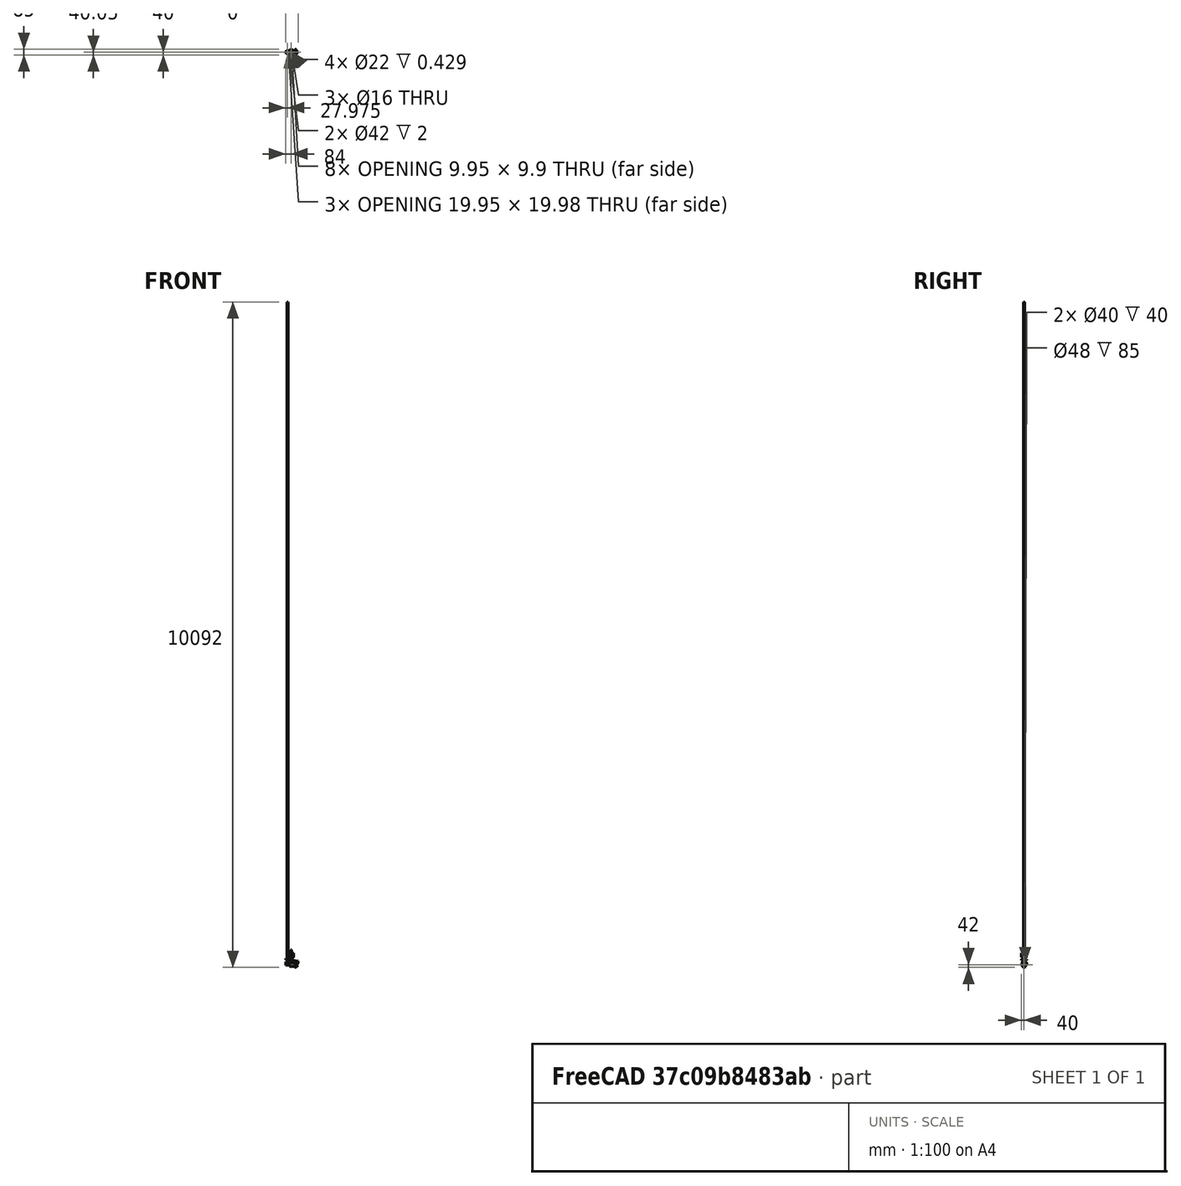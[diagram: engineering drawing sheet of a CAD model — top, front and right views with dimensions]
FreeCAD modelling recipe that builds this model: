
FCSTD DOCUMENT  (FreeCAD 0.16R6707 (Git))
Label: Mechanism-final
License: All rights reserved
LicenseURL: http://en.wikipedia.org/wiki/All_rights_reserved
objects: Sketcher::SketchObject×37, Part::Feature×23, PartDesign::Pad×16, App::DocumentObjectGroup×16, PartDesign::Revolution×13, Part::Sphere×10, Part::MultiFuse×9, Part::Cut×6, Part::Cylinder×4, Part::Part2DObjectPython×3, PartDesign::Pocket×1, Part::Sweep×1
note: 153 computed .brp shape members not serialized (recipe doc carries the construction recipe); baked Part::Feature solids carry a one-line shape summary decoded from their .brp

FEATURE [Part::Part2DObjectPython] InvoluteGear  # Draft 2D object (typed FeaturePython)
  ExternalGear = true
  HighPrecision = true
  Modules = 2.5
  NumberOfTeeth = 15
  Placement = pos=(0,0,20) rot=(0,0,1;0rad)
  PressureAngle = 20
FEATURE [PartDesign::Pad] Pad004  label="15-Teeth-Gear"
  Length = 10
  Length2 = 100
  Placement = pos=(0,0,20) rot=(0,0,1;0rad)
  Sketch = -> InvoluteGear
  Type = 0
FEATURE [Sketcher::SketchObject] Sketch004  label="15-Teeth-Gear-Hole-Sketch"
  Placement = pos=(0,0,20) rot=(1,0,0;3.14159rad)
  Support = -> Pad004 [Face151]
  sketch-geometry (4):
    g0: ArcOfCircle CenterX=0 CenterY=0 CenterZ=0 NormalX=0 NormalY=0 NormalZ=1 Radius=10 StartAngle=0.100167 EndAngle=6.18302
    g1: LineSegment StartX=9.94987 StartY=1 StartZ=0 EndX=8.94987 EndY=1 EndZ=0
    g2: LineSegment StartX=8.94987 StartY=1 StartZ=0 EndX=8.94987 EndY=-1 EndZ=0
    g3: LineSegment StartX=8.94987 StartY=-1 StartZ=0 EndX=9.94987 EndY=-1 EndZ=0
  constraints (12):
    c: Coincident(g0,g-1)
    c: Radius(g0) = 10
    c: Horizontal(g1)
    c: Coincident(g1,g2)
    c: Vertical(g2)
    c: Coincident(g2,g3)
    c: Symmetric(g1,g2,g-1)
    c: Horizontal(g3)
    c: Distance(g2) = 2
    c: Coincident(g0,g1)
    c: Coincident(g0,g3)
    c: Distance(g1) = 1
FEATURE [Sketcher::SketchObject] Sketch006  label="Main_Shaft_Sketch"
  Placement = pos=(0,0,0.5) rot=(0,0,1;0rad)
  sketch-geometry (4):
    g0: ArcOfCircle CenterX=0 CenterY=0 CenterZ=0 NormalX=0 NormalY=0 NormalZ=1 Radius=10 StartAngle=0.100167 EndAngle=6.18302
    g1: LineSegment StartX=9.94987 StartY=1 StartZ=0 EndX=8.94987 EndY=1 EndZ=0
    g2: LineSegment StartX=8.94987 StartY=1 StartZ=0 EndX=8.94987 EndY=-1 EndZ=0
    g3: LineSegment StartX=8.94987 StartY=-1 StartZ=0 EndX=9.94987 EndY=-1 EndZ=0
  constraints (12):
    c: Coincident(g0,g-1)
    c: Horizontal(g1)
    c: Coincident(g1,g2)
    c: Vertical(g2)
    c: Coincident(g2,g3)
    c: Horizontal(g3)
    c: Symmetric(g1,g2,g-1)
    c: Coincident(g0,g1)
    c: Coincident(g0,g3)
    c: Radius(g0) = 10
    c: DistanceX(g1,g1) = 1
    c: DistanceY(g2,g2) = 2
FEATURE [PartDesign::Pad] Pad005  label="Main_Shaft"
  Length = 90
  Length2 = 100
  Midplane = true
  Placement = pos=(0,0,0.5) rot=(0,0,1;0rad)
  Sketch = -> Sketch006
  Type = 0
FEATURE [Sketcher::SketchObject] Sketch007  label="Crank-Sketch"
  Placement = pos=(0,0,-35) rot=(0,0,1;0rad)
  sketch-geometry (10):
    g0: ArcOfCircle CenterX=0 CenterY=0 CenterZ=0 NormalX=0 NormalY=0 NormalZ=1 Radius=10 StartAngle=0.100167 EndAngle=6.18302
    g1: LineSegment StartX=9.94987 StartY=1 StartZ=0 EndX=8.94987 EndY=1 EndZ=0
    g2: LineSegment StartX=8.94987 StartY=1 StartZ=0 EndX=8.94987 EndY=-1 EndZ=0
    g3: LineSegment StartX=8.94987 StartY=-1 StartZ=0 EndX=9.94987 EndY=-1 EndZ=0
    g4: Circle CenterX=-20 CenterY=0 CenterZ=0 NormalX=0 NormalY=0 NormalZ=1 Radius=5
    g5: LineSegment [constr] StartX=-20 StartY=8 StartZ=0 EndX=-20 EndY=-8 EndZ=0
    g6: ArcOfCircle CenterX=-20 CenterY=0 CenterZ=0 NormalX=0 NormalY=0 NormalZ=1 Radius=8 StartAngle=1.5708 EndAngle=4.71239
    g7: ArcOfCircle CenterX=0 CenterY=0 CenterZ=0 NormalX=0 NormalY=0 NormalZ=1 Radius=20 StartAngle=4.71239 EndAngle=7.85398
    g8: ArcOfCircle CenterX=-24.2209 CenterY=37.7016 CenterZ=0 NormalX=0 NormalY=0 NormalZ=1 Radius=30 StartAngle=4.85356 EndAngle=5.65206
    g9: ArcOfCircle CenterX=-24.2209 CenterY=-37.7016 CenterZ=0 NormalX=0 NormalY=0 NormalZ=1 Radius=30 StartAngle=0.631124 EndAngle=1.42963
  constraints (31):
    c: Coincident(g0,g-1)
    c: Radius(g0) = 10
    c: Horizontal(g1)
    c: Coincident(g1,g2)
    c: Vertical(g2)
    c: Coincident(g2,g3)
    c: Horizontal(g3)
    c: Symmetric(g1,g2,g-1)
    c: Distance(g2) = 2
    c: Coincident(g0,g1)
    c: Coincident(g0,g3)
    c: Distance(g1) = 1
    c: Radius(g4) = 5
    c: Vertical(g5)
    c: PointOnObject(g4,g-1)
    c: DistanceX(g4,g-1) = 20
    c: PointOnObject(g4,g5)
    c: Coincident(g6,g4)
    c: Coincident(g6,g5)
    c: Coincident(g5,g6)
    c: Radius(g6) = 8
    c: Coincident(g7,g-1)
    c: PointOnObject(g7,g-2)
    c: PointOnObject(g7,g-2)
    c: Radius(g7) = 20
    c: Coincident(g8,g7)
    c: Coincident(g5,g8)
    c: Radius(g8) = 30
    c: Coincident(g9,g7)
    c: Coincident(g9,g5)
    c: Radius(g9) = 30
FEATURE [PartDesign::Pad] Pad006  label="Main-Crank"
  Length = 10
  Length2 = 100
  Placement = pos=(0,0,-35) rot=(0,0,1;0rad)
  Reversed = true
  Sketch = -> Sketch007
  Type = 0
FEATURE [Sketcher::SketchObject] Sketch008  label="Crank-Shaft"
  Placement = pos=(0,0,-35) rot=(0,0,1;0rad)
  sketch-geometry (1):
    g0: Circle CenterX=-20 CenterY=0 CenterZ=0 NormalX=0 NormalY=0 NormalZ=1 Radius=5
  constraints (3):
    c: PointOnObject(g0,g-1)
    c: DistanceX(g0,g-1) = 20
    c: Radius(g0) = 5
FEATURE [PartDesign::Pad] Pad007  label="Crank-Shaft001"
  Length = 20
  Length2 = 100
  Placement = pos=(0,0,-35) rot=(0,0,1;0rad)
  Reversed = true
  Sketch = -> Sketch008
  Type = 0
FEATURE [App::DocumentObjectGroup] Group003  label="Crank"
  Group = -> [Pad006,Pad007]
FEATURE [Sketcher::SketchObject] Sketch009  label="ConnRod-Sketch"
  Placement = pos=(0,0,-45) rot=(0,0,1;0rad)
  sketch-geometry (8):
    g0: Circle CenterX=-20 CenterY=0 CenterZ=0 NormalX=0 NormalY=0 NormalZ=1 Radius=5
    g1: LineSegment [constr] StartX=-20 StartY=8 StartZ=0 EndX=-20 EndY=-8 EndZ=0
    g2: Circle CenterX=40 CenterY=0 CenterZ=0 NormalX=0 NormalY=0 NormalZ=1 Radius=3
    g3: LineSegment [constr] StartX=40 StartY=5 StartZ=0 EndX=40 EndY=-5 EndZ=0
    g4: ArcOfCircle CenterX=40 CenterY=0 CenterZ=0 NormalX=0 NormalY=0 NormalZ=1 Radius=5 StartAngle=4.71239 EndAngle=7.85398
    g5: ArcOfCircle CenterX=-20 CenterY=0 CenterZ=0 NormalX=0 NormalY=0 NormalZ=1 Radius=8 StartAngle=1.5708 EndAngle=4.71239
    g6: ArcOfCircle CenterX=16.3162 CenterY=132.824 CenterZ=0 NormalX=0 NormalY=0 NormalZ=1 Radius=130 StartAngle=4.42927 EndAngle=4.8956
    g7: ArcOfCircle CenterX=16.3162 CenterY=-132.824 CenterZ=0 NormalX=0 NormalY=0 NormalZ=1 Radius=130 StartAngle=1.38759 EndAngle=1.85392
  constraints (24):
    c: PointOnObject(g0,g-1)
    c: Vertical(g1)
    c: PointOnObject(g0,g1)
    c: Radius(g0) = 5
    c: PointOnObject(g2,g-1)
    c: Radius(g2) = 3
    c: Vertical(g3)
    c: PointOnObject(g2,g3)
    c: Coincident(g4,g2)
    c: Coincident(g4,g3)
    c: Coincident(g4,g3)
    c: Radius(g4) = 5
    c: Coincident(g5,g0)
    c: Coincident(g5,g1)
    c: Coincident(g5,g1)
    c: Radius(g5) = 8
    c: DistanceX(g0,g-1) = 20
    c: DistanceX(g-1,g2) = 40
    c: Coincident(g6,g1)
    c: Coincident(g6,g3)
    c: Radius(g6) = 130
    c: Coincident(g7,g1)
    c: Coincident(g7,g3)
    c: Radius(g7) = 130
FEATURE [PartDesign::Pad] Pad008  label="ConnRod"
  Length = 10
  Length2 = 100
  Placement = pos=(0,0,-45) rot=(0,0,1;0rad)
  Reversed = true
  Sketch = -> Sketch009
  Type = 0
FEATURE [App::DocumentObjectGroup] Group004  label="Connecting-Rod"
  Group = -> [Pad008]
FEATURE [Sketcher::SketchObject] Sketch010  label="Piston-Sketch"
  Placement = pos=(0,0,-50) rot=(0,0,1;0rad)
  sketch-geometry (12):
    g0: LineSegment StartX=30 StartY=20 StartZ=0 EndX=70 EndY=20 EndZ=0
    g1: LineSegment StartX=30 StartY=20 StartZ=0 EndX=30 EndY=24 EndZ=0
    g2: LineSegment StartX=30 StartY=24 StartZ=0 EndX=64 EndY=24 EndZ=0
    g3: LineSegment StartX=64 StartY=24 StartZ=0 EndX=64 EndY=23 EndZ=0
    g4: LineSegment StartX=64 StartY=23 StartZ=0 EndX=66 EndY=23 EndZ=0
    g5: LineSegment StartX=66 StartY=23 StartZ=0 EndX=66 EndY=24 EndZ=0
    g6: LineSegment StartX=66 StartY=24 StartZ=0 EndX=72 EndY=24 EndZ=0
    g7: LineSegment [constr] StartX=64 StartY=24 StartZ=0 EndX=66 EndY=24 EndZ=0
    g8: ArcOfCircle CenterX=41.7122 CenterY=3.87375e-05 CenterZ=0 NormalX=0 NormalY=0 NormalZ=1 Radius=38.6438 StartAngle=6.28318 EndAngle=6.95327
    g9: LineSegment [constr] StartX=80.3561 StartY=0 StartZ=0 EndX=80.3561 EndY=16.6961 EndZ=0
    g10: LineSegment StartX=80.3561 StartY=0 StartZ=0 EndX=76.3561 EndY=0 EndZ=0
    g11: ArcOfCircle CenterX=41.7122 CenterY=3.87375e-05 CenterZ=0 NormalX=0 NormalY=0 NormalZ=1 Radius=34.6438 StartAngle=6.28318 EndAngle=6.89861
  constraints (35):
    c: Horizontal(g0)
    c: Coincident(g0,g1)
    c: Vertical(g1)
    c: Coincident(g1,g2)
    c: Horizontal(g2)
    c: Coincident(g2,g3)
    c: Coincident(g3,g4)
    c: Horizontal(g4)
    c: Coincident(g4,g5)
    c: Vertical(g5)
    c: Coincident(g5,g6)
    c: Horizontal(g6)
    c: Coincident(g7,g2)
    c: Coincident(g7,g5)
    c: Horizontal(g7)
    c: Vertical(g3)
    c: PointOnObject(g8,g-1)
    c: Coincident(g6,g8)
    c: Coincident(g9,g8)
    c: Vertical(g9)
    c: Tangent(g9,g8)
    c: DistanceY(g1,g1) = 4
    c: DistanceY(g3,g3) = 1
    c: Coincident(g10,g8)
    c: Horizontal(g10)
    c: Coincident(g11,g0)
    c: Coincident(g10,g11)
    c: DistanceX(g10,g10) = 4
    c: DistanceX(g4,g4) = 2
    c: DistanceX(g0,g0) = 40
    c: DistanceX(g0,g6) = 2
    c: Coincident(g8,g11)
    c: DistanceX(g6,g6) = 6
    c: DistanceX(g-1,g0) = 30
    c: DistanceY(g-1,g0) = 20
FEATURE [PartDesign::Revolution] Revolution  label="Main-Piston"
  Angle = 360
  Axis = (1,0,0)
  Base = (0,0,-50)
  Placement = pos=(0,0,-50) rot=(0,0,1;0rad)
  ReferenceAxis = -> Sketch010 [H_Axis]
  Sketch = -> Sketch010
FEATURE [Part::Part2DObjectPython] InvoluteGear001  # Draft 2D object (typed FeaturePython)
  ExternalGear = true
  HighPrecision = true
  Modules = 2.5
  NumberOfTeeth = 30
  Placement = pos=(56,0,20) rot=(0,0,1;0.10472rad)
  PressureAngle = 20
FEATURE [PartDesign::Pad] Pad009  label="Big-Gear"
  Length = 10
  Length2 = 100
  Placement = pos=(56,0,20) rot=(0,0,1;0.10472rad)
  Sketch = -> InvoluteGear001
  Type = 0
FEATURE [Sketcher::SketchObject] Sketch011  label="Shaft-Sketch"
  Placement = pos=(56,0,-15) rot=(0,0,1;0rad)
  sketch-geometry (4):
    g0: ArcOfCircle CenterX=0 CenterY=0 CenterZ=0 NormalX=0 NormalY=0 NormalZ=1 Radius=5 StartAngle=4.91375 EndAngle=10.7942
    g1: LineSegment StartX=-1 StartY=-4.89898 StartZ=0 EndX=-1 EndY=-3.89898 EndZ=0
    g2: LineSegment StartX=-1 StartY=-3.89898 StartZ=0 EndX=1 EndY=-3.89898 EndZ=0
    g3: LineSegment StartX=1 StartY=-3.89898 StartZ=0 EndX=1 EndY=-4.89898 EndZ=0
  constraints (12):
    c: Coincident(g0,g-1)
    c: Radius(g0) = 5
    c: Vertical(g1)
    c: Coincident(g1,g2)
    c: Horizontal(g2)
    c: Coincident(g2,g3)
    c: Vertical(g3)
    c: Symmetric(g1,g2,g-2)
    c: Distance(g2) = 2
    c: Coincident(g0,g3)
    c: Coincident(g0,g1)
    c: Distance(g1) = 1
FEATURE [PartDesign::Pad] Pad010  label="Shaft"
  Length = 190
  Length2 = 100
  Placement = pos=(56,0,-15) rot=(0,0,1;0rad)
  Sketch = -> Sketch011
  Type = 0
FEATURE [Sketcher::SketchObject] Sketch012  label="Issolator-Sketch"
  Placement = pos=(0,0,55) rot=(0,0,1;0rad)
  sketch-geometry (6):
    g0: ArcOfCircle CenterX=56 CenterY=0 CenterZ=0 NormalX=0 NormalY=0 NormalZ=1 Radius=5 StartAngle=4.91375 EndAngle=10.7942
    g1: LineSegment StartX=55 StartY=-4.89898 StartZ=0 EndX=55 EndY=-3.89898 EndZ=0
    g2: LineSegment StartX=55 StartY=-3.89898 StartZ=0 EndX=57 EndY=-3.89898 EndZ=0
    g3: LineSegment StartX=57 StartY=-3.89898 StartZ=0 EndX=57 EndY=-4.89898 EndZ=0
    g4: LineSegment [constr] StartX=56 StartY=0 StartZ=0 EndX=56 EndY=-2.78093 EndZ=0
    g5: Circle CenterX=56 CenterY=0 CenterZ=0 NormalX=0 NormalY=0 NormalZ=1 Radius=8
  constraints (17):
    c: PointOnObject(g0,g-1)
    c: Vertical(g1)
    c: Coincident(g1,g2)
    c: Horizontal(g2)
    c: Coincident(g2,g3)
    c: Vertical(g3)
    c: Coincident(g4,g0)
    c: Vertical(g4)
    c: Symmetric(g1,g2,g4)
    c: Distance(g2) = 2
    c: Coincident(g0,g3)
    c: Coincident(g0,g1)
    c: Distance(g1) = 1
    c: Radius(g0) = 5
    c: DistanceX(g-1,g0) = 56
    c: Coincident(g5,g0)
    c: Radius(g5) = 8
FEATURE [PartDesign::Pad] Pad011  label="Isolator"
  Length = 75
  Length2 = 100
  Placement = pos=(0,0,55) rot=(0,0,1;0rad)
  Sketch = -> Sketch012
  Type = 0
FEATURE [Sketcher::SketchObject] Sketch013  label="Coil-Core-Sketch"
  Placement = pos=(0,0,60) rot=(0,0,1;0rad)
  sketch-geometry (14):
    g0: LineSegment [constr] StartX=56 StartY=0 StartZ=0 EndX=56 EndY=10 EndZ=0
    g1: LineSegment [constr] StartX=56 StartY=0 StartZ=0 EndX=47.8085 EndY=5.73576 EndZ=0
    g2: LineSegment [constr] StartX=56 StartY=0 StartZ=0 EndX=64.1915 EndY=5.73576 EndZ=0
    g3: LineSegment StartX=47.8085 StartY=5.73576 StartZ=0 EndX=47.8085 EndY=31.8674 EndZ=0
    g4: LineSegment StartX=64.1915 StartY=5.73576 StartZ=0 EndX=64.1915 EndY=31.8674 EndZ=0
    g5: ArcOfCircle CenterX=56 CenterY=0 CenterZ=0 NormalX=0 NormalY=0 NormalZ=1 Radius=32.9034 StartAngle=1.8224 EndAngle=2.53073
    g6: ArcOfCircle CenterX=56 CenterY=0 CenterZ=0 NormalX=0 NormalY=0 NormalZ=1 Radius=32.9034 StartAngle=0.610865 EndAngle=1.31919
    g7: LineSegment StartX=29.0471 StartY=18.8726 StartZ=0 EndX=24.9513 EndY=21.7405 EndZ=0
    g8: LineSegment StartX=82.9529 StartY=18.8726 StartZ=0 EndX=87.0487 EndY=21.7405 EndZ=0
    g9: LineSegment [constr] StartX=64.1915 StartY=5.73576 StartZ=0 EndX=82.9529 EndY=18.8726 EndZ=0
    g10: LineSegment [constr] StartX=29.0471 StartY=18.8726 StartZ=0 EndX=47.8085 EndY=5.73576 EndZ=0
    g11: ArcOfCircle CenterX=56 CenterY=0 CenterZ=0 NormalX=0 NormalY=0 NormalZ=1 Radius=37.9034 StartAngle=0.610865 EndAngle=2.53073
    g12: ArcOfCircle CenterX=56 CenterY=0 CenterZ=0 NormalX=0 NormalY=0 NormalZ=1 Radius=10 StartAngle=2.53073 EndAngle=6.89405
    g13: Circle CenterX=56 CenterY=0 CenterZ=0 NormalX=0 NormalY=0 NormalZ=1 Radius=8
  constraints (37):
    c: PointOnObject(g0,g-1)
    c: Vertical(g0)
    c: Coincident(g1,g0)
    c: Coincident(g2,g0)
    c: Angle(g0,g1) = 0.959931
    c: Angle(g2,g0) = 0.959931
    c: Distance(g0) = 10
    c: Coincident(g3,g1)
    c: Vertical(g3)
    c: Coincident(g4,g2)
    c: Vertical(g4)
    c: Equal(g3,g4)
    c: Coincident(g5,g0)
    c: Coincident(g3,g5)
    c: Coincident(g6,g0)
    c: Coincident(g6,g4)
    c: Coincident(g7,g5)
    c: Coincident(g8,g6)
    c: Parallel(g8,g2)
    c: Coincident(g9,g2)
    c: Coincident(g9,g6)
    c: Parallel(g9,g2)
    c: Coincident(g10,g5)
    c: Coincident(g10,g1)
    c: Parallel(g10,g1)
    c: Parallel(g7,g1)
    c: Coincident(g11,g0)
    c: Coincident(g11,g7)
    c: Coincident(g11,g8)
    c: DistanceX(g-1,g0) = 56
    c: Distance(g7) = 5
    c: Equal(g1,g0)
    c: Coincident(g12,g0)
    c: Coincident(g12,g1)
    c: Coincident(g12,g2)
    c: Coincident(g13,g0)
    c: Radius(g13) = 8
FEATURE [PartDesign::Pad] Pad012  label="Coil-Core"
  Length = 65
  Length2 = 100
  Placement = pos=(0,0,60) rot=(0,0,1;0rad)
  Sketch = -> Sketch013
  Type = 0
FEATURE [Part::Feature] Pad012001  label="Coil-Core001"
  Placement = pos=(84,-48.4974,60) rot=(0,0,1;2.0944rad)
  shape: bbox 47.9 x 53.78 x 65 mm, 11 faces (baked)
FEATURE [Part::Feature] Pad012001001  label="Coil-Core002"
  Placement = pos=(84,48.4974,60) rot=(0,0,1;4.18879rad)
  shape: bbox 47.9 x 53.78 x 65 mm, 11 faces (baked)
FEATURE [Sketcher::SketchObject] Sketch014  label="Bearing1Sketch1"
  Placement = pos=(0,0,0) rot=(0.57735,0.57735,0.57735;2.0944rad)
  sketch-geometry (7):
    g0: LineSegment StartX=15 StartY=33 StartZ=0 EndX=10 EndY=33 EndZ=0
    g1: LineSegment StartX=10 StartY=33 StartZ=0 EndX=10 EndY=45 EndZ=0
    g2: LineSegment StartX=10 StartY=45 StartZ=0 EndX=15 EndY=45 EndZ=0
    g3: LineSegment StartX=15 StartY=33 StartZ=0 EndX=15 EndY=35 EndZ=0
    g4: LineSegment StartX=15 StartY=45 StartZ=0 EndX=15 EndY=43 EndZ=0
    g5: ArcOfCircle CenterX=18 CenterY=39 CenterZ=0 NormalX=0 NormalY=0 NormalZ=1 Radius=5 StartAngle=2.2143 EndAngle=4.06889
    g6: LineSegment [constr] StartX=18 StartY=39 StartZ=0 EndX=10 EndY=39 EndZ=0
  constraints (22):
    c: Horizontal(g0)
    c: Coincident(g0,g1)
    c: Vertical(g1)
    c: Coincident(g1,g2)
    c: Horizontal(g2)
    c: Equal(g0,g2)
    c: Coincident(g3,g0)
    c: Vertical(g3)
    c: Coincident(g4,g2)
    c: Vertical(g4)
    c: Coincident(g5,g3)
    c: Coincident(g4,g5)
    c: Coincident(g6,g5)
    c: PointOnObject(g6,g1)
    c: Symmetric(g0,g1,g6)
    c: DistanceY(g1,g1) = 12
    c: DistanceX(g2,g2) = 5
    c: DistanceY(g-1,g1) = 45
    c: Equal(g3,g4)
    c: DistanceY(g3,g3) = 2
    c: DistanceX(g-1,g1) = 10
    c: Radius(g5) = 5
FEATURE [PartDesign::Revolution] Revolution001  label="Inner-Revolution"
  Angle = 360
  Axis = (0,0,1)
  Base = (0,0,0)
  Placement = pos=(0,0,0) rot=(0.57735,0.57735,0.57735;2.0944rad)
  ReferenceAxis = -> Sketch014 [V_Axis]
  Reversed = true
  Sketch = -> Sketch014
FEATURE [Part::Sphere] Sphere
  Angle1 = -90
  Angle2 = 90
  Angle3 = 360
  Placement = pos=(0,18,39) rot=(0,0,1;0rad)
  Radius = 5
FEATURE [Part::Sphere] Sphere001
  Angle1 = -90
  Angle2 = 90
  Angle3 = 360
  Placement = pos=(0,-18,39) rot=(0,0,1;0rad)
  Radius = 5
FEATURE [Part::Sphere] Sphere002
  Angle1 = -90
  Angle2 = 90
  Angle3 = 360
  Placement = pos=(18,0,39) rot=(0,0,1;0rad)
  Radius = 5
FEATURE [Part::Sphere] Sphere003
  Angle1 = -90
  Angle2 = 90
  Angle3 = 360
  Placement = pos=(-18,0,39) rot=(0,0,1;0rad)
  Radius = 5
FEATURE [Part::MultiFuse] Fusion
  Shapes = -> [Sphere003,Sphere002,Sphere001,Sphere]
FEATURE [Part::Feature] Fusion001
  Placement = pos=(0,0,0) rot=(0,0,-1;0.785398rad)
  shape: bbox 35.46 x 35.46 x 10 mm, 4 faces, 4 solids (baked)
FEATURE [Part::MultiFuse] Fusion002  label="Balls"
  Shapes = -> [Fusion,Fusion001]
FEATURE [Sketcher::SketchObject] Sketch015  label="Bearing1Sketch002"
  Placement = pos=(0,0,0) rot=(0.57735,0.57735,0.57735;2.0944rad)
  sketch-geometry (7):
    g0: LineSegment StartX=26 StartY=33 StartZ=0 EndX=26 EndY=45 EndZ=0
    g1: LineSegment StartX=21 StartY=33 StartZ=0 EndX=21 EndY=35 EndZ=0
    g2: LineSegment StartX=21 StartY=45 StartZ=0 EndX=21 EndY=43 EndZ=0
    g3: LineSegment [constr] StartX=18 StartY=39 StartZ=0 EndX=26 EndY=39 EndZ=0
    g4: LineSegment StartX=26 StartY=33 StartZ=0 EndX=21 EndY=33 EndZ=0
    g5: LineSegment StartX=26 StartY=45 StartZ=0 EndX=21 EndY=45 EndZ=0
    g6: ArcOfCircle CenterX=18 CenterY=39 CenterZ=0 NormalX=0 NormalY=0 NormalZ=1 Radius=5 StartAngle=5.35589 EndAngle=7.21048
  constraints (21):
    c: Vertical(g0)
    c: Vertical(g1)
    c: Vertical(g2)
    c: PointOnObject(g3,g0)
    c: Symmetric(g0,g0,g3)
    c: DistanceY(g0,g0) = 12
    c: DistanceY(g-1,g0) = 45
    c: Equal(g1,g2)
    c: DistanceY(g1,g1) = 2
    c: Coincident(g4,g0)
    c: Coincident(g4,g1)
    c: Horizontal(g4)
    c: Coincident(g5,g0)
    c: Coincident(g5,g2)
    c: Horizontal(g5)
    c: DistanceX(g5,g5) = 5
    c: Coincident(g6,g3)
    c: Coincident(g6,g2)
    c: Coincident(g1,g6)
    c: Radius(g6) = 5
    c: DistanceX(g-1,g1) = 21
FEATURE [PartDesign::Revolution] Revolution002  label="Autside-Revolution"
  Angle = 360
  Axis = (0,0,1)
  Base = (0,0,0)
  Placement = pos=(0,0,0) rot=(0.57735,0.57735,0.57735;2.0944rad)
  ReferenceAxis = -> Sketch015 [V_Axis]
  Reversed = true
  Sketch = -> Sketch015
FEATURE [App::DocumentObjectGroup] Group008  label="Bearing1"
  Group = -> [Revolution001,Fusion002,Revolution002]
FEATURE [Sketcher::SketchObject] Sketch016  label="Bearing1Sketch003"
  Placement = pos=(0,0,-52) rot=(0.57735,0.57735,0.57735;2.0944rad)
  sketch-geometry (7):
    g0: LineSegment StartX=15 StartY=33 StartZ=0 EndX=10 EndY=33 EndZ=0
    g1: LineSegment StartX=10 StartY=33 StartZ=0 EndX=10 EndY=45 EndZ=0
    g2: LineSegment StartX=10 StartY=45 StartZ=0 EndX=15 EndY=45 EndZ=0
    g3: LineSegment StartX=15 StartY=33 StartZ=0 EndX=15 EndY=35 EndZ=0
    g4: LineSegment StartX=15 StartY=45 StartZ=0 EndX=15 EndY=43 EndZ=0
    g5: ArcOfCircle CenterX=18 CenterY=39 CenterZ=0 NormalX=0 NormalY=0 NormalZ=1 Radius=5 StartAngle=2.2143 EndAngle=4.06889
    g6: LineSegment [constr] StartX=18 StartY=39 StartZ=0 EndX=10 EndY=39 EndZ=0
  constraints (22):
    c: Horizontal(g0)
    c: Coincident(g0,g1)
    c: Vertical(g1)
    c: Coincident(g1,g2)
    c: Horizontal(g2)
    c: Equal(g0,g2)
    c: Coincident(g3,g0)
    c: Vertical(g3)
    c: Coincident(g4,g2)
    c: Vertical(g4)
    c: Coincident(g5,g3)
    c: Coincident(g4,g5)
    c: Coincident(g6,g5)
    c: PointOnObject(g6,g1)
    c: Symmetric(g0,g1,g6)
    c: DistanceY(g1,g1) = 12
    c: DistanceX(g2,g2) = 5
    c: DistanceY(g-1,g1) = 45
    c: Equal(g3,g4)
    c: DistanceY(g3,g3) = 2
    c: DistanceX(g-1,g1) = 10
    c: Radius(g5) = 5
FEATURE [PartDesign::Revolution] Revolution003  label="Inner-Revolution001"
  Angle = 360
  Axis = (0,0,1)
  Base = (0,0,-52)
  Placement = pos=(0,0,-52) rot=(0.57735,0.57735,0.57735;2.0944rad)
  ReferenceAxis = -> Sketch016 [V_Axis]
  Reversed = true
  Sketch = -> Sketch016
FEATURE [Part::Sphere] Sphere004
  Angle1 = -90
  Angle2 = 90
  Angle3 = 360
  Placement = pos=(0,18,39) rot=(0,0,1;0rad)
  Radius = 5
FEATURE [Part::Sphere] Sphere005
  Angle1 = -90
  Angle2 = 90
  Angle3 = 360
  Placement = pos=(0,-18,39) rot=(0,0,1;0rad)
  Radius = 5
FEATURE [Part::Sphere] Sphere006
  Angle1 = -90
  Angle2 = 90
  Angle3 = 360
  Placement = pos=(18,0,39) rot=(0,0,1;0rad)
  Radius = 5
FEATURE [Part::Sphere] Sphere007
  Angle1 = -90
  Angle2 = 90
  Angle3 = 360
  Placement = pos=(-18,0,39) rot=(0,0,1;0rad)
  Radius = 5
FEATURE [Part::MultiFuse] Fusion003
  Shapes = -> [Sphere007,Sphere006,Sphere005,Sphere004]
FEATURE [Part::Feature] Fusion004
  Placement = pos=(0,0,0) rot=(0,0,-1;0.785398rad)
  shape: bbox 35.46 x 35.46 x 10 mm, 4 faces, 4 solids (baked)
FEATURE [Part::MultiFuse] Fusion005  label="Balls001"
  Placement = pos=(0,0,-52) rot=(0,0,1;0rad)
  Shapes = -> [Fusion003,Fusion004]
FEATURE [Sketcher::SketchObject] Sketch017  label="Bearing1Sketch004"
  Placement = pos=(0,0,-52) rot=(0.57735,0.57735,0.57735;2.0944rad)
  sketch-geometry (7):
    g0: LineSegment StartX=26 StartY=33 StartZ=0 EndX=26 EndY=45 EndZ=0
    g1: LineSegment StartX=21 StartY=33 StartZ=0 EndX=21 EndY=35 EndZ=0
    g2: LineSegment StartX=21 StartY=45 StartZ=0 EndX=21 EndY=43 EndZ=0
    g3: LineSegment [constr] StartX=18 StartY=39 StartZ=0 EndX=26 EndY=39 EndZ=0
    g4: LineSegment StartX=26 StartY=33 StartZ=0 EndX=21 EndY=33 EndZ=0
    g5: LineSegment StartX=26 StartY=45 StartZ=0 EndX=21 EndY=45 EndZ=0
    g6: ArcOfCircle CenterX=18 CenterY=39 CenterZ=0 NormalX=0 NormalY=0 NormalZ=1 Radius=5 StartAngle=5.35589 EndAngle=7.21048
  constraints (21):
    c: Vertical(g0)
    c: Vertical(g1)
    c: Vertical(g2)
    c: PointOnObject(g3,g0)
    c: Symmetric(g0,g0,g3)
    c: DistanceY(g0,g0) = 12
    c: DistanceY(g-1,g0) = 45
    c: Equal(g1,g2)
    c: DistanceY(g1,g1) = 2
    c: Coincident(g4,g0)
    c: Coincident(g4,g1)
    c: Horizontal(g4)
    c: Coincident(g5,g0)
    c: Coincident(g5,g2)
    c: Horizontal(g5)
    c: DistanceX(g5,g5) = 5
    c: Coincident(g6,g3)
    c: Coincident(g6,g2)
    c: Coincident(g1,g6)
    c: Radius(g6) = 5
    c: DistanceX(g-1,g1) = 21
FEATURE [PartDesign::Revolution] Revolution004  label="Autside-Revolution001"
  Angle = 270
  Axis = (0,0,1)
  Base = (0,0,-52)
  Placement = pos=(0,0,-52) rot=(0.57735,0.57735,0.57735;2.0944rad)
  ReferenceAxis = -> Sketch017 [V_Axis]
  Reversed = true
  Sketch = -> Sketch017
FEATURE [App::DocumentObjectGroup] Group009  label="Bearing2"
  Group = -> [Revolution003,Fusion005,Revolution004]
FEATURE [Sketcher::SketchObject] Sketch018  label="Coil-Wire-1"
  Placement = pos=(56,7,0) rot=(1,0,0;1.5708rad)
  sketch-geometry (4):
    g0: ArcOfCircle CenterX=0 CenterY=62.2611 CenterZ=0 NormalX=0 NormalY=0 NormalZ=1 Radius=10 StartAngle=3.14159 EndAngle=6.28319
    g1: ArcOfCircle CenterX=0 CenterY=122.261 CenterZ=0 NormalX=0 NormalY=0 NormalZ=1 Radius=10 StartAngle=0 EndAngle=3.14159
    g2: LineSegment StartX=10 StartY=62.2611 StartZ=0 EndX=10 EndY=122.261 EndZ=0
    g3: LineSegment StartX=-10 StartY=62.2611 StartZ=0 EndX=-10 EndY=122.261 EndZ=0
  constraints (9):
    c: Tangent(g0,g3) = 1.5708
    c: Tangent(g0,g2) = -1.5708
    c: Tangent(g2,g1) = -1.5708
    c: Tangent(g3,g1) = 1.5708
    c: Vertical(g2)
    c: Equal(g0,g1)
    c: DistanceY(g2,g2) = 60
    c: Radius(g0) = 10
    c: PointOnObject(g0,g-2)
FEATURE [Part::Cylinder] Cylinder
  Angle = 360
  Height = 49
  Placement = pos=(40,0,-75) rot=(0,0,1;0rad)
  Radius = 3
FEATURE [Part::Cut] Cut  label="Piston-Hole"
  Base = -> Revolution
  Tool = -> Cylinder
FEATURE [Part::Cylinder] Cylinder001
  Angle = 360
  Height = 46
  Placement = pos=(40,0,-73) rot=(0,0,1;0rad)
  Radius = 3
FEATURE [App::DocumentObjectGroup] Group005  label="Piston"
  Group = -> [Cut,Cylinder001]
FEATURE [Sketcher::SketchObject] Sketch019  label="Cilinder-Main-Sketch"
  Placement = pos=(30,0,0) rot=(0.57735,0.57735,0.57735;2.0944rad)
  sketch-geometry (2):
    g0: Circle CenterX=0 CenterY=-50 CenterZ=0 NormalX=0 NormalY=0 NormalZ=1 Radius=24
    g1: Circle CenterX=0 CenterY=-50 CenterZ=0 NormalX=0 NormalY=0 NormalZ=1 Radius=28
  constraints (5):
    c: Radius(g0) = 24
    c: PointOnObject(g0,g-2)
    c: DistanceY(g0,g-1) = 50
    c: Coincident(g1,g0)
    c: Radius(g1) = 28
FEATURE [PartDesign::Pad] Pad012001002  label="MainCylinder"
  Length = 85
  Length2 = 100
  Placement = pos=(30,0,0) rot=(0.57735,0.57735,0.57735;2.0944rad)
  Sketch = -> Sketch019
  Type = 0
FEATURE [App::DocumentObjectGroup] Group010  label="Cilinder"
  Group = -> [Pad012001002]
FEATURE [Sketcher::SketchObject] Sketch020  label="CrankShaftAnimationSketch"
  Placement = pos=(0,0,-55) rot=(0,0,1;0rad)
  sketch-geometry (2):
    g0: LineSegment StartX=0 StartY=0 StartZ=0 EndX=-20 EndY=0 EndZ=0
    g1: LineSegment StartX=-20 StartY=0 StartZ=0 EndX=40 EndY=0 EndZ=0
  constraints (8):
    c: Coincident(g0,g-1)
    c: Distance(g0) = 20
    c: Coincident(g1,g0)
    c: Distance(g1) = 60
    c: DistanceX(g1,g-1) = -40
    c: Angle(g-1,g1) = 3.14159
    c: Angle(g0,g-1) = 3.14159
    c: PointOnObject(g1,g-1)
FEATURE [Part::Feature] Fusion006001  label="PistonFinal"
  shape: bbox 50.36 x 48 x 48 mm, 14 faces (baked)
FEATURE [Part::Feature] Pad008001  label="ConnRodFinal"
  Placement = pos=(0,0,-45) rot=(0,0,1;0rad)
  shape: bbox 73 x 16 x 10 mm, 8 faces (baked)
FEATURE [Part::Feature] Fusion006002002002001  label="Balls1"
  shape: bbox 46 x 46 x 62 mm, 16 faces, 16 solids (baked)
FEATURE [PartDesign::Pocket] Pocket  label="15-Teeth-Gear-Hole"
  Length = 5
  Placement = pos=(0,0,20) rot=(0,0,1;0rad)
  Sketch = -> Sketch004
  Type = 1
FEATURE [App::DocumentObjectGroup] Group002  label="Main-Gear"
  Group = -> [Pad004,Pad005,Pocket]
FEATURE [Sketcher::SketchObject] Sketch
  Placement = pos=(56,0,0) rot=(0,0,1;0rad)
  sketch-geometry (11):
    g0: ArcOfCircle CenterX=0 CenterY=0 CenterZ=0 NormalX=0 NormalY=0 NormalZ=1 Radius=5 StartAngle=4.91375 EndAngle=10.7942
    g1: LineSegment StartX=-1 StartY=-3.89898 StartZ=0 EndX=1 EndY=-3.89898 EndZ=0
    g2: LineSegment StartX=15 StartY=0 StartZ=0 EndX=15 EndY=-10 EndZ=0
    g3: LineSegment StartX=0 StartY=-15 StartZ=0 EndX=10 EndY=-15 EndZ=0
    g4: ArcOfCircle CenterX=10 CenterY=-10 CenterZ=0 NormalX=0 NormalY=0 NormalZ=1 Radius=5 StartAngle=4.71239 EndAngle=6.28319
    g5: LineSegment StartX=1 StartY=-4.89898 StartZ=0 EndX=1 EndY=-3.89898 EndZ=0
    g6: LineSegment StartX=-1 StartY=-3.89898 StartZ=0 EndX=-1 EndY=-4.89898 EndZ=0
    g7: ArcOfCircle CenterX=0 CenterY=0 CenterZ=0 NormalX=0 NormalY=0 NormalZ=1 Radius=15 StartAngle=0 EndAngle=4.71239
    g8: LineSegment [constr] StartX=0 StartY=0 StartZ=0 EndX=15 EndY=-6.30178 EndZ=0
    g9: LineSegment [constr] StartX=0 StartY=0 StartZ=0 EndX=13.4703 EndY=-13.5996 EndZ=0
    g10: LineSegment [constr] StartX=0 StartY=0 StartZ=0 EndX=4.28538 EndY=-15 EndZ=0
  constraints (32):
    c: PointOnObject(g0,g-1)
    c: Radius(g0) = 5
    c: Horizontal(g1)
    c: DistanceX(g1,g1) = 2
    c: Vertical(g2)
    c: Horizontal(g3)
    c: Coincident(g4,g2)
    c: Coincident(g4,g3)
    c: Tangent(g4,g2,g2) = 1.5708
    c: Tangent(g4,g3)
    c: Coincident(g0,g-1)
    c: Symmetric(g0,g0,g-2)
    c: Coincident(g5,g0)
    c: Coincident(g5,g1)
    c: Vertical(g5)
    c: DistanceY(g5,g5) = 1
    c: Coincident(g6,g1)
    c: Coincident(g6,g0)
    c: Vertical(g6)
    c: DistanceX(g-1,g4) = 10
    c: Coincident(g7,g-1)
    c: Coincident(g7,g2)
    c: Coincident(g7,g3)
    c: PointOnObject(g3,g-2)
    c: PointOnObject(g2,g-1)
    c: Radius(g7) = 15
    c: Coincident(g8,g-1)
    c: PointOnObject(g8,g2)
    c: Coincident(g9,g-1)
    c: PointOnObject(g9,g4)
    c: Coincident(g10,g-1)
    c: PointOnObject(g10,g3)
FEATURE [Part::Cut] Cut001  label="Big-Gear-Hole"
  Base = -> Pad009
  Tool = -> Pad010
FEATURE [App::DocumentObjectGroup] Group006  label="DC-Rotor"
  Group = -> [Pad011,Pad012,Pad012001,Pad012001001,Sketch018,Cut001]
FEATURE [PartDesign::Pad] Pad  label="Rotor"
  Length = 10
  Length2 = 100
  Midplane = true
  Placement = pos=(56,0,0) rot=(0,0,1;0rad)
  Sketch = -> Sketch
  Type = 0
FEATURE [Sketcher::SketchObject] Sketch021  label="Valve1CalculationSketch"
  Placement = pos=(56,0,-5) rot=(0,0,1;0rad)
  sketch-geometry (11):
    g0: ArcOfCircle CenterX=0 CenterY=0 CenterZ=0 NormalX=0 NormalY=0 NormalZ=1 Radius=5 StartAngle=4.91375 EndAngle=10.7942
    g1: LineSegment StartX=-1 StartY=-3.89898 StartZ=0 EndX=1 EndY=-3.89898 EndZ=0
    g2: LineSegment StartX=15 StartY=0 StartZ=0 EndX=15 EndY=-10 EndZ=0
    g3: LineSegment StartX=0 StartY=-15 StartZ=0 EndX=10 EndY=-15 EndZ=0
    g4: ArcOfCircle CenterX=10 CenterY=-10 CenterZ=0 NormalX=0 NormalY=0 NormalZ=1 Radius=5 StartAngle=4.71239 EndAngle=6.28319
    g5: LineSegment StartX=1 StartY=-4.89898 StartZ=0 EndX=1 EndY=-3.89898 EndZ=0
    g6: LineSegment StartX=-1 StartY=-3.89898 StartZ=0 EndX=-1 EndY=-4.89898 EndZ=0
    g7: ArcOfCircle CenterX=0 CenterY=0 CenterZ=0 NormalX=0 NormalY=0 NormalZ=1 Radius=15 StartAngle=0 EndAngle=4.71239
    g8: LineSegment [constr] StartX=0 StartY=0 StartZ=0 EndX=15 EndY=-9.74111 EndZ=0
    g9: LineSegment [constr] StartX=0 StartY=0 StartZ=0 EndX=10.1167 EndY=-14.9986 EndZ=0
    g10: LineSegment [constr] StartX=0 StartY=0 StartZ=0 EndX=0 EndY=-15 EndZ=0
  constraints (37):
    c: Radius(g0) = 5
    c: Horizontal(g1)
    c: DistanceX(g1,g1) = 2
    c: Vertical(g2)
    c: Horizontal(g3)
    c: Coincident(g4,g2)
    c: Coincident(g4,g3)
    c: Tangent(g4,g2,g2) = 1.5708
    c: Tangent(g4,g3)
    c: Coincident(g5,g0)
    c: Coincident(g5,g1)
    c: Vertical(g5)
    c: DistanceY(g5,g5) = 1
    c: Coincident(g6,g1)
    c: Coincident(g6,g0)
    c: Vertical(g6)
    c: DistanceX(g-1,g4) = 10
    c: Coincident(g7,g-1)
    c: Coincident(g7,g2)
    c: Coincident(g7,g3)
    c: PointOnObject(g3,g-2)
    c: PointOnObject(g2,g-1)
    c: Radius(g7) = 15
    c: Coincident(g8,g-1)
    c: PointOnObject(g8,g2)
    c: Angle(g8,g-1) = 0.575959
    c: Distance(g8) = 17.8854
    c: Coincident(g9,g-1)
    c: PointOnObject(g9,g4)
    c: Coincident(g0,g-1)
    c: Symmetric(g1,g1,g-2)
    c: Angle(g9,g-1) = 0.977384
    c: Distance(g9) = 18.0916
    c: Coincident(g10,g-1)
    c: PointOnObject(g10,g3)
    c: Angle(g10,g-1) = 1.5708
    c: Distance(g10) = 15
FEATURE [Sketcher::SketchObject] Sketch022  label="Valve1-Rod-Sketch"
  Placement = pos=(71,0,0) rot=(0,0,1;0rad)
  sketch-geometry (10):
    g0: LineSegment StartX=3 StartY=3 StartZ=0 EndX=6 EndY=3 EndZ=0
    g1: LineSegment StartX=6 StartY=3 StartZ=0 EndX=6 EndY=5 EndZ=0
    g2: LineSegment StartX=6 StartY=5 StartZ=0 EndX=7 EndY=5 EndZ=0
    g3: LineSegment StartX=7 StartY=5 StartZ=0 EndX=7 EndY=3 EndZ=0
    g4: LineSegment StartX=7 StartY=3 StartZ=0 EndX=79 EndY=3 EndZ=0
    g5: LineSegment [constr] StartX=6 StartY=3 StartZ=0 EndX=7 EndY=3 EndZ=0
    g6: ArcOfCircle CenterX=3 CenterY=0 CenterZ=0 NormalX=0 NormalY=0 NormalZ=1 Radius=3 StartAngle=1.5708 EndAngle=3.14159
    g7: LineSegment [constr] StartX=3 StartY=0 StartZ=0 EndX=3 EndY=3 EndZ=0
    g8: LineSegment StartX=79 StartY=3 StartZ=0 EndX=79 EndY=0 EndZ=0
    g9: LineSegment StartX=0 StartY=0 StartZ=0 EndX=79 EndY=0 EndZ=0
  constraints (28):
    c: Horizontal(g0)
    c: Coincident(g0,g1)
    c: Vertical(g1)
    c: Coincident(g1,g2)
    c: Horizontal(g2)
    c: Coincident(g2,g3)
    c: Coincident(g3,g4)
    c: Horizontal(g4)
    c: Coincident(g5,g0)
    c: Horizontal(g5)
    c: Coincident(g3,g5)
    c: Vertical(g3)
    c: DistanceX(g2,g2) = 1
    c: DistanceY(g3,g3) = 2
    c: PointOnObject(g6,g-1)
    c: Coincident(g6,g0)
    c: Coincident(g6,g-1)
    c: Radius(g6) = 3
    c: DistanceX(g0,g0) = 3
    c: Coincident(g7,g6)
    c: Coincident(g7,g0)
    c: Vertical(g7)
    c: DistanceX(g4,g4) = 72
    c: Coincident(g8,g4)
    c: PointOnObject(g8,g-1)
    c: Vertical(g8)
    c: Coincident(g9,g-1)
    c: Coincident(g9,g8)
FEATURE [PartDesign::Revolution] Revolution005  label="Valve1-Rod"
  Angle = 360
  Axis = (1,0,0)
  Base = (71,0,0)
  Placement = pos=(71,0,0) rot=(0,0,1;0rad)
  ReferenceAxis = -> Sketch022 [H_Axis]
  Sketch = -> Sketch022
FEATURE [Part::Feature] Fusion006002002002002001  label="MainShaft"
  shape: bbox 49.25 x 42.41 x 100.5 mm, 188 faces (baked)
FEATURE [Sketcher::SketchObject] Sketch023
  Placement = pos=(56,0,0) rot=(0.57735,0.57735,0.57735;2.0944rad)
  sketch-geometry (7):
    g0: LineSegment StartX=5 StartY=-8 StartZ=0 EndX=5 EndY=-14 EndZ=0
    g1: ArcOfCircle CenterX=9.54615 CenterY=-11 CenterZ=0 NormalX=0 NormalY=0 NormalZ=1 Radius=3 StartAngle=2.11225 EndAngle=4.17093
    g2: LineSegment [constr] StartX=9.54615 StartY=-11 StartZ=0 EndX=19.5864 EndY=-11 EndZ=0
    g3: LineSegment StartX=8 StartY=-8.42912 StartZ=0 EndX=8 EndY=-8 EndZ=0
    g4: LineSegment StartX=8 StartY=-8 StartZ=0 EndX=5 EndY=-8 EndZ=0
    g5: LineSegment StartX=5 StartY=-14 StartZ=0 EndX=8 EndY=-14 EndZ=0
    g6: LineSegment StartX=8 StartY=-14 StartZ=0 EndX=8 EndY=-13.5709 EndZ=0
  constraints (21):
    c: Vertical(g0)
    c: DistanceX(g-1,g0) = 5
    c: Horizontal(g2)
    c: Coincident(g1,g2)
    c: DistanceY(g0,g-1) = 8
    c: Coincident(g1,g3)
    c: Vertical(g3)
    c: Coincident(g4,g3)
    c: Coincident(g4,g0)
    c: Horizontal(g4)
    c: Coincident(g0,g5)
    c: Horizontal(g5)
    c: Coincident(g5,g6)
    c: Coincident(g6,g1)
    c: Vertical(g6)
    c: Equal(g4,g5)
    c: Radius(g1) = 3
    c: DistanceX(g5,g5) = 3
    c: DistanceY(g0,g0) = 6
    c: Equal(g3,g6)
    c: DistanceY(g3,g3) = 0.429123
FEATURE [PartDesign::Revolution] Revolution005002  label="Inner-Revolution002"
  Angle = 360
  Axis = (0,0,1)
  Base = (56,0,0)
  Placement = pos=(56,0,0) rot=(0.57735,0.57735,0.57735;2.0944rad)
  ReferenceAxis = -> Sketch023 [V_Axis]
  Reversed = true
  Sketch = -> Sketch023
FEATURE [Part::Sphere] Sphere008
  Angle1 = -90
  Angle2 = 90
  Angle3 = 360
  Placement = pos=(56,9.5,-11) rot=(0,0,1;0rad)
  Radius = 3
FEATURE [Part::Sphere] Sphere009
  Angle1 = -90
  Angle2 = 90
  Angle3 = 360
  Placement = pos=(56,-9.5,-11) rot=(0,0,1;0rad)
  Radius = 3
FEATURE [Part::MultiFuse] Fusion006002002002002002002002
  Shapes = -> [Sphere008,Sphere009]
FEATURE [Part::Feature] Fusion006002002002002002002002001  label="Fusion006002002002002002002003"
  Placement = pos=(56,56,0) rot=(0,0,-1;1.5708rad)
  shape: bbox 25 x 6 x 6 mm, 2 faces, 2 solids (baked)
FEATURE [Part::Feature] Fusion006002002002002002002002002  label="Fusion006002002002002002002004"
  Placement = pos=(16.402,39.598,0) rot=(0,0,-1;0.785398rad)
  shape: bbox 19.44 x 19.44 x 6 mm, 2 faces, 2 solids (baked)
FEATURE [Part::Feature] Fusion006002002002002002002002003  label="Fusion006002002002002002002005"
  Placement = pos=(16.402,-39.598,0) rot=(0,0,1;0.785398rad)
  shape: bbox 19.44 x 19.44 x 6 mm, 2 faces, 2 solids (baked)
FEATURE [Part::MultiFuse] Fusion006002002002002002002002004
  Shapes = -> [Fusion006002002002002002002002,Fusion006002002002002002002002001,Fusion006002002002002002002002002,Fusion006002002002002002002002003]
FEATURE [Part::Feature] Fusion006002002002002002002002005001  label="SecondaryShaft1"
  shape: bbox 79.74 x 80.01 x 190 mm, 370 faces (baked)
FEATURE [Part::Feature] Fusion006002002002002002002002005002001  label="Balls2"
  shape: bbox 25 x 25 x 60 mm, 16 faces, 16 solids (baked)
FEATURE [Sketcher::SketchObject] Sketch024
  Placement = pos=(56,0,0) rot=(0.57735,0.57735,0.57735;2.0944rad)
  sketch-geometry (7):
    g0: LineSegment StartX=-14 StartY=-8 StartZ=0 EndX=-14 EndY=-14 EndZ=0
    g1: ArcOfCircle CenterX=-9.45385 CenterY=-11 CenterZ=0 NormalX=0 NormalY=0 NormalZ=1 Radius=3 StartAngle=2.11225 EndAngle=4.17093
    g2: LineSegment [constr] StartX=-9.45385 StartY=-11 StartZ=0 EndX=19.5864 EndY=-11 EndZ=0
    g3: LineSegment StartX=-11 StartY=-8.42912 StartZ=0 EndX=-11 EndY=-8 EndZ=0
    g4: LineSegment StartX=-11 StartY=-8 StartZ=0 EndX=-14 EndY=-8 EndZ=0
    g5: LineSegment StartX=-14 StartY=-14 StartZ=0 EndX=-11 EndY=-14 EndZ=0
    g6: LineSegment StartX=-11 StartY=-14 StartZ=0 EndX=-11 EndY=-13.5709 EndZ=0
  constraints (21):
    c: Vertical(g0)
    c: Horizontal(g2)
    c: Coincident(g1,g2)
    c: DistanceY(g0,g-1) = 8
    c: Coincident(g1,g3)
    c: Vertical(g3)
    c: Coincident(g4,g3)
    c: Coincident(g4,g0)
    c: Horizontal(g4)
    c: Coincident(g0,g5)
    c: Horizontal(g5)
    c: Coincident(g5,g6)
    c: Coincident(g6,g1)
    c: Vertical(g6)
    c: Equal(g4,g5)
    c: Radius(g1) = 3
    c: DistanceY(g0,g0) = 6
    c: Equal(g3,g6)
    c: DistanceY(g3,g3) = 0.429123
    c: DistanceX(g5,g5) = 3
    c: DistanceX(g5,g-1) = 11
FEATURE [PartDesign::Revolution] Revolution005003
  Angle = 360
  Axis = (0,0,1)
  Base = (56,0,0)
  Placement = pos=(56,0,0) rot=(0.57735,0.57735,0.57735;2.0944rad)
  ReferenceAxis = -> Sketch024 [V_Axis]
  Sketch = -> Sketch024
FEATURE [Sketcher::SketchObject] Sketch025
  Placement = pos=(115,0,-50) rot=(1,0,0;1.5708rad)
  sketch-geometry (11):
    g0: LineSegment StartX=0 StartY=35 StartZ=0 EndX=0 EndY=24 EndZ=0
    g1: LineSegment StartX=0 StartY=35 StartZ=0 EndX=17 EndY=35 EndZ=0
    g2: LineSegment StartX=0 StartY=24 StartZ=0 EndX=4.94977 EndY=4 EndZ=0
    g3: LineSegment StartX=17 StartY=35 StartZ=0 EndX=19.8829 EndY=23.3514 EndZ=0
    g4: LineSegment StartX=19.8829 StartY=23.3514 StartZ=0 EndX=27.6486 EndY=25.2734 EndZ=0
    g5: LineSegment StartX=27.6486 StartY=25.2734 StartZ=0 EndX=30.051 EndY=15.5662 EndZ=0
    g6: LineSegment StartX=30.051 StartY=15.5662 StartZ=0 EndX=22.2853 EndY=13.6443 EndZ=0
    g7: LineSegment StartX=22.2853 StartY=13.6443 StartZ=0 EndX=24.6721 EndY=4 EndZ=0
    g8: LineSegment StartX=24.6721 StartY=4 StartZ=0 EndX=4.94977 EndY=4 EndZ=0
    g9: LineSegment [constr] StartX=19.8829 StartY=23.3514 StartZ=0 EndX=22.2853 EndY=13.6443 EndZ=0
    g10: LineSegment [constr] StartX=28.8498 StartY=20.4198 StartZ=0 EndX=2.5 EndY=13.8985 EndZ=0
  constraints (33):
    c: Vertical(g0)
    c: DistanceY(g-1,g0) = 24
    c: PointOnObject(g0,g-2)
    c: DistanceY(g-1,g0) = 35
    c: Coincident(g1,g0)
    c: Horizontal(g1)
    c: PointOnObject(g2,g-2)
    c: Coincident(g0,g2)
    c: DistanceY(g-1,g2) = 4
    c: Coincident(g1,g3)
    c: Coincident(g3,g4)
    c: Coincident(g4,g5)
    c: Coincident(g6,g7)
    c: Coincident(g7,g8)
    c: Coincident(g8,g2)
    c: Horizontal(g8)
    c: Parallel(g7,g2)
    c: Parallel(g5,g2)
    c: Coincident(g5,g6)
    c: Parallel(g4,g6)
    c: DistanceX(g1,g1) = 17
    c: Coincident(g9,g3)
    c: Coincident(g9,g6)
    c: Parallel(g3,g9)
    c: Parallel(g9,g7)
    c: Perpendicular(g6,g5)
    c: Distance(g9) = 10
    c: PointOnObject(g10,g5)
    c: PointOnObject(g10,g2)
    c: Symmetric(g5,g4,g10)
    c: Distance(g3) = 12
    c: Distance(g6) = 8
    c: DistanceX(g-1,g10) = 2.5
FEATURE [PartDesign::Revolution] Revolution005004  label="Main"
  Angle = 360
  Axis = (1,0,0)
  Base = (115,0,-50)
  Placement = pos=(115,0,-50) rot=(1,0,0;1.5708rad)
  ReferenceAxis = -> Sketch025 [H_Axis]
  Sketch = -> Sketch025
FEATURE [Sketcher::SketchObject] Sketch027  label="Valve1-Sketch"
  Placement = pos=(115,0,-50) rot=(1,0,0;1.5708rad)
  sketch-geometry (17):
    g0: LineSegment [constr] StartX=0 StartY=35 StartZ=0 EndX=0 EndY=24 EndZ=0
    g1: LineSegment [constr] StartX=0 StartY=35 StartZ=0 EndX=15 EndY=35 EndZ=0
    g2: LineSegment [constr] StartX=0 StartY=24 StartZ=0 EndX=5.12635 EndY=4 EndZ=0
    g3: LineSegment [constr] StartX=15 StartY=35 StartZ=0 EndX=17.9795 EndY=23.3758 EndZ=0
    g4: LineSegment [constr] StartX=17.9795 StartY=23.3758 StartZ=0 EndX=29.6037 EndY=26.3553 EndZ=0
    g5: LineSegment [constr] StartX=29.6037 StartY=26.3553 StartZ=0 EndX=32.0866 EndY=16.6684 EndZ=0
    g6: LineSegment [constr] StartX=32.0866 StartY=16.6684 StartZ=0 EndX=20.4624 EndY=13.6889 EndZ=0
    g7: LineSegment [constr] StartX=20.4624 StartY=13.6889 StartZ=0 EndX=22.9458 EndY=4 EndZ=0
    g8: LineSegment [constr] StartX=22.9458 StartY=4 StartZ=0 EndX=5.12635 EndY=4 EndZ=0
    g9: LineSegment [constr] StartX=17.9795 StartY=23.3758 StartZ=0 EndX=20.4624 EndY=13.6889 EndZ=0
    g10: LineSegment [constr] StartX=30.8452 StartY=21.5118 StartZ=0 EndX=2.5 EndY=14.2465 EndZ=0
    g11: LineSegment StartX=2.5 StartY=14.2465 StartZ=0 EndX=1.01025 EndY=20.0586 EndZ=0
    g12: LineSegment StartX=1.01025 StartY=20.0586 StartZ=0 EndX=2.00013 EndY=19.9166 EndZ=0
    g13: LineSegment StartX=2.00013 StartY=19.9166 StartZ=0 EndX=3.94079 EndY=16.6804 EndZ=0
    g14: LineSegment StartX=3.94079 StartY=16.6804 StartZ=0 EndX=36.8761 EndY=25.1223 EndZ=0
    g15: LineSegment StartX=36.8761 StartY=25.1223 StartZ=0 EndX=37.3727 EndY=23.185 EndZ=0
    g16: LineSegment StartX=37.3727 StartY=23.185 StartZ=0 EndX=2.5 EndY=14.2465 EndZ=0
  constraints (50):
    c: Vertical(g0)
    c: DistanceY(g-1,g0) = 24
    c: PointOnObject(g0,g-2)
    c: DistanceY(g-1,g0) = 35
    c: Coincident(g1,g0)
    c: Horizontal(g1)
    c: PointOnObject(g2,g-2)
    c: Coincident(g0,g2)
    c: DistanceY(g-1,g2) = 4
    c: Coincident(g1,g3)
    c: Coincident(g3,g4)
    c: Coincident(g4,g5)
    c: Coincident(g6,g7)
    c: Coincident(g7,g8)
    c: Coincident(g8,g2)
    c: Horizontal(g8)
    c: Parallel(g7,g2)
    c: Parallel(g5,g2)
    c: Coincident(g5,g6)
    c: Parallel(g4,g6)
    c: DistanceX(g1,g1) = 15
    c: Coincident(g9,g3)
    c: Coincident(g9,g6)
    c: Parallel(g3,g9)
    c: Parallel(g9,g7)
    c: Perpendicular(g6,g5)
    c: Distance(g9) = 10
    c: PointOnObject(g10,g5)
    c: PointOnObject(g10,g2)
    c: Symmetric(g5,g4,g10)
    c: Distance(g3) = 12
    c: Distance(g6) = 12
    c: DistanceX(g-1,g10) = 2.5
    c: PointOnObject(g11,g2)
    c: Coincident(g11,g10)
    c: Coincident(g12,g11)
    c: Coincident(g12,g13)
    c: Coincident(g13,g14)
    c: Coincident(g14,g15)
    c: Coincident(g15,g16)
    c: Coincident(g16,g10)
    c: PointOnObject(g10,g16)
    c: Perpendicular(g16,g15)
    c: Parallel(g14,g16)
    c: Distance(g15) = 2
    c: Distance(g12) = 1
    c: Distance(g10,g11) = 6
    c: Distance(g16) = 36
    c: Distance(g14) = 34
    c: Distance(g13) = 3.77348
FEATURE [PartDesign::Revolution] Revolution005005  label="Valve002"
  Angle = 360
  Axis = (-28.3452,0,-7.26537)
  Base = (145.845,0,-28.4882)
  Placement = pos=(115,0,-50) rot=(1,0,0;1.5708rad)
  ReferenceAxis = -> Sketch027 [Axis10]
  Reversed = true
  Sketch = -> Sketch027
FEATURE [App::DocumentObjectGroup] Group011  label="Valve1"
  Group = -> [Pad,Revolution005,Sketch021,Revolution005005]
FEATURE [Sketcher::SketchObject] Sketch028  label="Valve1-Sketch001"
  Placement = pos=(115,0,-50) rot=(1,0,0;1.5708rad)
  sketch-geometry (22):
    g0: LineSegment [constr] StartX=0 StartY=35 StartZ=0 EndX=0 EndY=24 EndZ=0
    g1: LineSegment [constr] StartX=0 StartY=35 StartZ=0 EndX=15 EndY=35 EndZ=0
    g2: LineSegment [constr] StartX=0 StartY=24 StartZ=0 EndX=5.12635 EndY=4 EndZ=0
    g3: LineSegment [constr] StartX=15 StartY=35 StartZ=0 EndX=17.9795 EndY=23.3758 EndZ=0
    g4: LineSegment [constr] StartX=17.9795 StartY=23.3758 StartZ=0 EndX=29.6037 EndY=26.3553 EndZ=0
    g5: LineSegment [constr] StartX=29.6037 StartY=26.3553 StartZ=0 EndX=32.0866 EndY=16.6684 EndZ=0
    g6: LineSegment [constr] StartX=32.0866 StartY=16.6684 StartZ=0 EndX=20.4624 EndY=13.6889 EndZ=0
    g7: LineSegment [constr] StartX=20.4624 StartY=13.6889 StartZ=0 EndX=22.9458 EndY=4 EndZ=0
    g8: LineSegment [constr] StartX=22.9458 StartY=4 StartZ=0 EndX=5.12635 EndY=4 EndZ=0
    g9: LineSegment [constr] StartX=17.9795 StartY=23.3758 StartZ=0 EndX=20.4624 EndY=13.6889 EndZ=0
    g10: LineSegment [constr] StartX=30.8452 StartY=21.5118 StartZ=0 EndX=2.5 EndY=14.2465 EndZ=0
    g11: LineSegment [constr] StartX=2.5 StartY=14.2465 StartZ=0 EndX=1.01025 EndY=20.0586 EndZ=0
    g12: LineSegment StartX=1.01025 StartY=20.0586 StartZ=0 EndX=2.00013 EndY=19.9167 EndZ=0
    g13: LineSegment StartX=2.00013 StartY=19.9167 StartZ=0 EndX=2.59937 EndY=18.9174 EndZ=0
    g14: LineSegment StartX=36.8761 StartY=25.1223 StartZ=0 EndX=37.3727 EndY=23.185 EndZ=0
    g15: LineSegment StartX=37.3727 StartY=23.185 StartZ=0 EndX=2.5 EndY=14.2465 EndZ=0
    g16: LineSegment StartX=1.01025 StartY=20.0586 StartZ=0 EndX=0.186608 EndY=19.8475 EndZ=0
    g17: LineSegment StartX=0.186608 StartY=19.8475 StartZ=0 EndX=1.6615 EndY=14.0316 EndZ=0
    g18: LineSegment StartX=1.6615 StartY=14.0316 StartZ=0 EndX=2.5 EndY=14.2465 EndZ=0
    g19: LineSegment StartX=2.59937 StartY=18.9174 StartZ=0 EndX=17.1296 EndY=22.6418 EndZ=0
    g20: LineSegment StartX=17.1296 StartY=22.6418 StartZ=0 EndX=17.7504 EndY=20.2201 EndZ=0
    g21: LineSegment StartX=17.7504 StartY=20.2201 StartZ=0 EndX=36.8761 EndY=25.1223 EndZ=0
  constraints (62):
    c: Vertical(g0)
    c: DistanceY(g-1,g0) = 24
    c: PointOnObject(g0,g-2)
    c: DistanceY(g-1,g0) = 35
    c: Coincident(g1,g0)
    c: Horizontal(g1)
    c: PointOnObject(g2,g-2)
    c: Coincident(g0,g2)
    c: DistanceY(g-1,g2) = 4
    c: Coincident(g1,g3)
    c: Coincident(g3,g4)
    c: Coincident(g4,g5)
    c: Coincident(g6,g7)
    c: Coincident(g7,g8)
    c: Coincident(g8,g2)
    c: Horizontal(g8)
    c: Parallel(g7,g2)
    c: Parallel(g5,g2)
    c: Coincident(g5,g6)
    c: Parallel(g4,g6)
    c: DistanceX(g1,g1) = 15
    c: Coincident(g9,g3)
    c: Coincident(g9,g6)
    c: Parallel(g3,g9)
    c: Parallel(g9,g7)
    c: Perpendicular(g6,g5)
    c: Distance(g9) = 10
    c: PointOnObject(g10,g5)
    c: PointOnObject(g10,g2)
    c: Symmetric(g5,g4,g10)
    c: Distance(g3) = 12
    c: Distance(g6) = 12
    c: DistanceX(g-1,g10) = 2.5
    c: Coincident(g11,g10)
    c: Coincident(g12,g11)
    c: Coincident(g12,g13)
    c: Coincident(g14,g15)
    c: Coincident(g15,g10)
    c: PointOnObject(g10,g15)
    c: Perpendicular(g15,g14)
    c: Distance(g14) = 2
    c: Distance(g12) = 1
    c: Distance(g10,g11) = 6
    c: Distance(g15) = 36
    c: PointOnObject(g11,g2)
    c: Coincident(g16,g11)
    c: Coincident(g16,g17)
    c: Coincident(g17,g18)
    c: Coincident(g10,g18)
    c: Parallel(g10,g18)
    c: Perpendicular(g2,g16)
    c: Coincident(g20,g19)
    c: Parallel(g20,g9)
    c: Distance(g20) = 2.5
    c: Coincident(g21,g20)
    c: Coincident(g21,g14)
    c: Distance(g21) = 19.744
    c: Coincident(g13,g19)
    c: Distance(g13) = 1.16516
    c: Parallel(g15,g21)
    c: Angle(g12,g13) = 2.25338
    c: Angle(g16,g12) = 2.74828
FEATURE [PartDesign::Revolution] Revolution005006  label="Valve1Hole001"
  Angle = 360
  Axis = (-28.3452,0,-7.26537)
  Base = (145.845,0,-28.4882)
  Placement = pos=(115,0,-50) rot=(1,0,0;1.5708rad)
  ReferenceAxis = -> Sketch028 [Axis10]
  Reversed = true
  Sketch = -> Sketch028
FEATURE [Part::Cut] Cut002  label="Valve1Hole"
  Base = -> Revolution005004
  Tool = -> Revolution005006
FEATURE [Part::Feature] Revolution005005001  label="ScapeValve"
  Placement = pos=(115,0,-50) rot=(1,0,0;1.5708rad)
  shape: bbox 36.86 x 12 x 16.69 mm, 5 faces (baked)
FEATURE [Part::Feature] Revolution005003001  label="Revolution005004"
  Placement = pos=(56,0,54) rot=(0.57735,0.57735,0.57735;2.0944rad)
  shape: bbox 28 x 28 x 6 mm, 6 faces (baked)
FEATURE [App::DocumentObjectGroup] Group012  label="Bearing3"
  Group = -> [Revolution005002,Fusion006002002002002002002002004,Revolution005003,Revolution005003001]
FEATURE [App::DocumentObjectGroup] Group007  label="Bearings"
  Group = -> [Group008,Group009,Group012]
FEATURE [Sketcher::SketchObject] Sketch029
  Placement = pos=(56,0,0) rot=(0,0,1;0rad)
  sketch-geometry (11):
    g0: ArcOfCircle CenterX=0 CenterY=0 CenterZ=0 NormalX=0 NormalY=0 NormalZ=1 Radius=5 StartAngle=4.91375 EndAngle=10.7942
    g1: LineSegment StartX=-1 StartY=-3.89898 StartZ=0 EndX=1 EndY=-3.89898 EndZ=0
    g2: LineSegment StartX=15 StartY=0 StartZ=0 EndX=15 EndY=-10 EndZ=0
    g3: LineSegment StartX=0 StartY=-15 StartZ=0 EndX=10 EndY=-15 EndZ=0
    g4: ArcOfCircle CenterX=10 CenterY=-10 CenterZ=0 NormalX=0 NormalY=0 NormalZ=1 Radius=5 StartAngle=4.71239 EndAngle=6.28319
    g5: LineSegment StartX=1 StartY=-4.89898 StartZ=0 EndX=1 EndY=-3.89898 EndZ=0
    g6: LineSegment StartX=-1 StartY=-3.89898 StartZ=0 EndX=-1 EndY=-4.89898 EndZ=0
    g7: ArcOfCircle CenterX=0 CenterY=0 CenterZ=0 NormalX=0 NormalY=0 NormalZ=1 Radius=15 StartAngle=0 EndAngle=4.71239
    g8: LineSegment [constr] StartX=0 StartY=0 StartZ=0 EndX=15 EndY=-3.968 EndZ=0
    g9: LineSegment [constr] StartX=0 StartY=0 StartZ=0 EndX=14.0725 EndY=-12.9009 EndZ=0
    g10: LineSegment [constr] StartX=0 StartY=0 StartZ=0 EndX=5.74529 EndY=-15 EndZ=0
  constraints (32):
    c: PointOnObject(g0,g-1)
    c: Radius(g0) = 5
    c: Horizontal(g1)
    c: DistanceX(g1,g1) = 2
    c: Vertical(g2)
    c: Horizontal(g3)
    c: Coincident(g4,g2)
    c: Coincident(g4,g3)
    c: Tangent(g4,g2,g2) = 1.5708
    c: Tangent(g4,g3)
    c: Coincident(g0,g-1)
    c: Symmetric(g0,g0,g-2)
    c: Coincident(g5,g0)
    c: Coincident(g5,g1)
    c: Vertical(g5)
    c: DistanceY(g5,g5) = 1
    c: Coincident(g6,g1)
    c: Coincident(g6,g0)
    c: Vertical(g6)
    c: DistanceX(g-1,g4) = 10
    c: Coincident(g7,g-1)
    c: Coincident(g7,g2)
    c: Coincident(g7,g3)
    c: PointOnObject(g3,g-2)
    c: PointOnObject(g2,g-1)
    c: Radius(g7) = 15
    c: Coincident(g8,g-1)
    c: PointOnObject(g8,g2)
    c: Coincident(g9,g-1)
    c: PointOnObject(g9,g4)
    c: Coincident(g10,g-1)
    c: PointOnObject(g10,g3)
FEATURE [Sketcher::SketchObject] Sketch030  label="Valve2-Sketch"
  Placement = pos=(115,0,-50) rot=(-1,0,0;1.5708rad)
  sketch-geometry (17):
    g0: LineSegment [constr] StartX=0 StartY=35 StartZ=0 EndX=0 EndY=24 EndZ=0
    g1: LineSegment [constr] StartX=0 StartY=35 StartZ=0 EndX=15 EndY=35 EndZ=0
    g2: LineSegment [constr] StartX=0 StartY=24 StartZ=0 EndX=5.12635 EndY=4 EndZ=0
    g3: LineSegment [constr] StartX=15 StartY=35 StartZ=0 EndX=17.9795 EndY=23.3758 EndZ=0
    g4: LineSegment [constr] StartX=17.9795 StartY=23.3758 StartZ=0 EndX=29.6037 EndY=26.3553 EndZ=0
    g5: LineSegment [constr] StartX=29.6037 StartY=26.3553 StartZ=0 EndX=32.0866 EndY=16.6684 EndZ=0
    g6: LineSegment [constr] StartX=32.0866 StartY=16.6684 StartZ=0 EndX=20.4624 EndY=13.6889 EndZ=0
    g7: LineSegment [constr] StartX=20.4624 StartY=13.6889 StartZ=0 EndX=22.9458 EndY=4 EndZ=0
    g8: LineSegment [constr] StartX=22.9458 StartY=4 StartZ=0 EndX=5.12635 EndY=4 EndZ=0
    g9: LineSegment [constr] StartX=17.9795 StartY=23.3758 StartZ=0 EndX=20.4624 EndY=13.6889 EndZ=0
    g10: LineSegment [constr] StartX=30.8452 StartY=21.5118 StartZ=0 EndX=2.5 EndY=14.2465 EndZ=0
    g11: LineSegment StartX=2.5 StartY=14.2465 StartZ=0 EndX=1.01025 EndY=20.0586 EndZ=0
    g12: LineSegment StartX=1.01025 StartY=20.0586 StartZ=0 EndX=2.00013 EndY=19.9166 EndZ=0
    g13: LineSegment StartX=2.00013 StartY=19.9166 StartZ=0 EndX=3.94079 EndY=16.6804 EndZ=0
    g14: LineSegment StartX=3.94079 StartY=16.6804 StartZ=0 EndX=36.8761 EndY=25.1223 EndZ=0
    g15: LineSegment StartX=36.8761 StartY=25.1223 StartZ=0 EndX=37.3727 EndY=23.185 EndZ=0
    g16: LineSegment StartX=37.3727 StartY=23.185 StartZ=0 EndX=2.5 EndY=14.2465 EndZ=0
  constraints (50):
    c: Vertical(g0)
    c: DistanceY(g-1,g0) = 24
    c: PointOnObject(g0,g-2)
    c: DistanceY(g-1,g0) = 35
    c: Coincident(g1,g0)
    c: Horizontal(g1)
    c: PointOnObject(g2,g-2)
    c: Coincident(g0,g2)
    c: DistanceY(g-1,g2) = 4
    c: Coincident(g1,g3)
    c: Coincident(g3,g4)
    c: Coincident(g4,g5)
    c: Coincident(g6,g7)
    c: Coincident(g7,g8)
    c: Coincident(g8,g2)
    c: Horizontal(g8)
    c: Parallel(g7,g2)
    c: Parallel(g5,g2)
    c: Coincident(g5,g6)
    c: Parallel(g4,g6)
    c: DistanceX(g1,g1) = 15
    c: Coincident(g9,g3)
    c: Coincident(g9,g6)
    c: Parallel(g3,g9)
    c: Parallel(g9,g7)
    c: Perpendicular(g6,g5)
    c: Distance(g9) = 10
    c: PointOnObject(g10,g5)
    c: PointOnObject(g10,g2)
    c: Symmetric(g5,g4,g10)
    c: Distance(g3) = 12
    c: Distance(g6) = 12
    c: DistanceX(g-1,g10) = 2.5
    c: PointOnObject(g11,g2)
    c: Coincident(g11,g10)
    c: Coincident(g12,g11)
    c: Coincident(g12,g13)
    c: Coincident(g13,g14)
    c: Coincident(g14,g15)
    c: Coincident(g15,g16)
    c: Coincident(g16,g10)
    c: PointOnObject(g10,g16)
    c: Perpendicular(g16,g15)
    c: Parallel(g14,g16)
    c: Distance(g15) = 2
    c: Distance(g12) = 1
    c: Distance(g10,g11) = 6
    c: Distance(g16) = 36
    c: Distance(g14) = 34
    c: Distance(g13) = 3.77348
FEATURE [PartDesign::Revolution] Revolution005005002  label="Valve003"
  Angle = 360
  Axis = (-28.3452,0,7.26537)
  Base = (145.845,0,-71.5118)
  Placement = pos=(115,0,-50) rot=(-1,0,0;1.5708rad)
  ReferenceAxis = -> Sketch030 [Axis10]
  Reversed = true
  Sketch = -> Sketch030
FEATURE [Part::Feature] Revolution005005002001  label="IntakeValve"
  Placement = pos=(114.998,0,-49.9994) rot=(-1,0,0;1.5708rad)
  shape: bbox 36.86 x 12 x 16.69 mm, 5 faces (baked)
FEATURE [Sketcher::SketchObject] Sketch031  label="Valve2-Sketch002"
  Placement = pos=(115,0,-50) rot=(-1,0,0;1.5708rad)
  sketch-geometry (22):
    g0: LineSegment [constr] StartX=0 StartY=35 StartZ=0 EndX=0 EndY=24 EndZ=0
    g1: LineSegment [constr] StartX=0 StartY=35 StartZ=0 EndX=15 EndY=35 EndZ=0
    g2: LineSegment [constr] StartX=0 StartY=24 StartZ=0 EndX=5.12635 EndY=4 EndZ=0
    g3: LineSegment [constr] StartX=15 StartY=35 StartZ=0 EndX=17.9795 EndY=23.3758 EndZ=0
    g4: LineSegment [constr] StartX=17.9795 StartY=23.3758 StartZ=0 EndX=29.6037 EndY=26.3553 EndZ=0
    g5: LineSegment [constr] StartX=29.6037 StartY=26.3553 StartZ=0 EndX=32.0866 EndY=16.6684 EndZ=0
    g6: LineSegment [constr] StartX=32.0866 StartY=16.6684 StartZ=0 EndX=20.4624 EndY=13.6889 EndZ=0
    g7: LineSegment [constr] StartX=20.4624 StartY=13.6889 StartZ=0 EndX=22.9458 EndY=4 EndZ=0
    g8: LineSegment [constr] StartX=22.9458 StartY=4 StartZ=0 EndX=5.12635 EndY=4 EndZ=0
    g9: LineSegment [constr] StartX=17.9795 StartY=23.3758 StartZ=0 EndX=20.4624 EndY=13.6889 EndZ=0
    g10: LineSegment [constr] StartX=30.8452 StartY=21.5118 StartZ=0 EndX=2.5 EndY=14.2465 EndZ=0
    g11: LineSegment [constr] StartX=2.5 StartY=14.2465 StartZ=0 EndX=1.01025 EndY=20.0586 EndZ=0
    g12: LineSegment StartX=1.01025 StartY=20.0586 StartZ=0 EndX=2.00013 EndY=19.9167 EndZ=0
    g13: LineSegment StartX=2.00013 StartY=19.9167 StartZ=0 EndX=2.59937 EndY=18.9174 EndZ=0
    g14: LineSegment StartX=36.8761 StartY=25.1223 StartZ=0 EndX=37.3727 EndY=23.185 EndZ=0
    g15: LineSegment StartX=37.3727 StartY=23.185 StartZ=0 EndX=2.5 EndY=14.2465 EndZ=0
    g16: LineSegment StartX=1.01025 StartY=20.0586 StartZ=0 EndX=0.186608 EndY=19.8475 EndZ=0
    g17: LineSegment StartX=0.186608 StartY=19.8475 StartZ=0 EndX=1.6615 EndY=14.0316 EndZ=0
    g18: LineSegment StartX=1.6615 StartY=14.0316 StartZ=0 EndX=2.5 EndY=14.2465 EndZ=0
    g19: LineSegment StartX=2.59937 StartY=18.9174 StartZ=0 EndX=17.1296 EndY=22.6418 EndZ=0
    g20: LineSegment StartX=17.1296 StartY=22.6418 StartZ=0 EndX=17.7504 EndY=20.2201 EndZ=0
    g21: LineSegment StartX=17.7504 StartY=20.2201 StartZ=0 EndX=36.8761 EndY=25.1223 EndZ=0
  constraints (62):
    c: Vertical(g0)
    c: DistanceY(g-1,g0) = 24
    c: PointOnObject(g0,g-2)
    c: DistanceY(g-1,g0) = 35
    c: Coincident(g1,g0)
    c: Horizontal(g1)
    c: PointOnObject(g2,g-2)
    c: Coincident(g0,g2)
    c: DistanceY(g-1,g2) = 4
    c: Coincident(g1,g3)
    c: Coincident(g3,g4)
    c: Coincident(g4,g5)
    c: Coincident(g6,g7)
    c: Coincident(g7,g8)
    c: Coincident(g8,g2)
    c: Horizontal(g8)
    c: Parallel(g7,g2)
    c: Parallel(g5,g2)
    c: Coincident(g5,g6)
    c: Parallel(g4,g6)
    c: DistanceX(g1,g1) = 15
    c: Coincident(g9,g3)
    c: Coincident(g9,g6)
    c: Parallel(g3,g9)
    c: Parallel(g9,g7)
    c: Perpendicular(g6,g5)
    c: Distance(g9) = 10
    c: PointOnObject(g10,g5)
    c: PointOnObject(g10,g2)
    c: Symmetric(g5,g4,g10)
    c: Distance(g3) = 12
    c: Distance(g6) = 12
    c: DistanceX(g-1,g10) = 2.5
    c: Coincident(g11,g10)
    c: Coincident(g12,g11)
    c: Coincident(g12,g13)
    c: Coincident(g14,g15)
    c: Coincident(g15,g10)
    c: PointOnObject(g10,g15)
    c: Perpendicular(g15,g14)
    c: Distance(g14) = 2
    c: Distance(g12) = 1
    c: Distance(g10,g11) = 6
    c: Distance(g15) = 36
    c: PointOnObject(g11,g2)
    c: Coincident(g16,g11)
    c: Coincident(g16,g17)
    c: Coincident(g17,g18)
    c: Coincident(g10,g18)
    c: Parallel(g10,g18)
    c: Perpendicular(g2,g16)
    c: Coincident(g20,g19)
    c: Parallel(g20,g9)
    c: Distance(g20) = 2.5
    c: Coincident(g21,g20)
    c: Coincident(g21,g14)
    c: Distance(g21) = 19.744
    c: Coincident(g13,g19)
    c: Distance(g13) = 1.16516
    c: Parallel(g15,g21)
    c: Angle(g12,g13) = 2.25338
    c: Angle(g16,g12) = 2.74828
FEATURE [PartDesign::Revolution] Revolution005005002002
  Angle = 360
  Axis = (-28.3452,0,7.26537)
  Base = (145.845,0,-71.5118)
  Placement = pos=(115,0,-50) rot=(-1,0,0;1.5708rad)
  ReferenceAxis = -> Sketch031 [Axis10]
  Reversed = true
  Sketch = -> Sketch031
FEATURE [Part::Cut] Cut003
  Base = -> Cut002
  Tool = -> Revolution005005002002
FEATURE [Sketcher::SketchObject] Sketch032
  Placement = pos=(56,0,0) rot=(0,0,1;0rad)
  sketch-geometry (11):
    g0: ArcOfCircle CenterX=0 CenterY=0 CenterZ=0 NormalX=0 NormalY=0 NormalZ=1 Radius=5 StartAngle=4.91375 EndAngle=10.7942
    g1: LineSegment StartX=-1 StartY=-3.89898 StartZ=0 EndX=1 EndY=-3.89898 EndZ=0
    g2: LineSegment StartX=15 StartY=0 StartZ=0 EndX=15 EndY=-10 EndZ=0
    g3: LineSegment StartX=0 StartY=-15 StartZ=0 EndX=10 EndY=-15 EndZ=0
    g4: ArcOfCircle CenterX=10 CenterY=-10 CenterZ=0 NormalX=0 NormalY=0 NormalZ=1 Radius=5 StartAngle=4.71239 EndAngle=6.28319
    g5: LineSegment StartX=1 StartY=-4.89898 StartZ=0 EndX=1 EndY=-3.89898 EndZ=0
    g6: LineSegment StartX=-1 StartY=-3.89898 StartZ=0 EndX=-1 EndY=-4.89898 EndZ=0
    g7: ArcOfCircle CenterX=0 CenterY=0 CenterZ=0 NormalX=0 NormalY=0 NormalZ=1 Radius=15 StartAngle=0 EndAngle=4.71239
    g8: LineSegment [constr] StartX=0 StartY=0 StartZ=0 EndX=15 EndY=-3.968 EndZ=0
    g9: LineSegment [constr] StartX=0 StartY=0 StartZ=0 EndX=14.0725 EndY=-12.9009 EndZ=0
    g10: LineSegment [constr] StartX=0 StartY=0 StartZ=0 EndX=5.74529 EndY=-15 EndZ=0
  constraints (32):
    c: PointOnObject(g0,g-1)
    c: Radius(g0) = 5
    c: Horizontal(g1)
    c: DistanceX(g1,g1) = 2
    c: Vertical(g2)
    c: Horizontal(g3)
    c: Coincident(g4,g2)
    c: Coincident(g4,g3)
    c: Tangent(g4,g2,g2) = 1.5708
    c: Tangent(g4,g3)
    c: Coincident(g0,g-1)
    c: Symmetric(g0,g0,g-2)
    c: Coincident(g5,g0)
    c: Coincident(g5,g1)
    c: Vertical(g5)
    c: DistanceY(g5,g5) = 1
    c: Coincident(g6,g1)
    c: Coincident(g6,g0)
    c: Vertical(g6)
    c: DistanceX(g-1,g4) = 10
    c: Coincident(g7,g-1)
    c: Coincident(g7,g2)
    c: Coincident(g7,g3)
    c: PointOnObject(g3,g-2)
    c: PointOnObject(g2,g-1)
    c: Radius(g7) = 15
    c: Coincident(g8,g-1)
    c: PointOnObject(g8,g2)
    c: Coincident(g9,g-1)
    c: PointOnObject(g9,g4)
    c: Coincident(g10,g-1)
    c: PointOnObject(g10,g3)
FEATURE [Sketcher::SketchObject] Sketch033
  Placement = pos=(56,0,11) rot=(0,0,1;0rad)
  sketch-geometry (8):
    g0: ArcOfCircle CenterX=0 CenterY=0 CenterZ=0 NormalX=0 NormalY=0 NormalZ=1 Radius=5 StartAngle=4.91375 EndAngle=10.7942
    g1: LineSegment StartX=-1 StartY=-3.89898 StartZ=0 EndX=1 EndY=-3.89898 EndZ=0
    g2: ArcOfCircle CenterX=-10 CenterY=-10 CenterZ=0 NormalX=0 NormalY=0 NormalZ=1 Radius=5 StartAngle=3.14159 EndAngle=4.71239
    g3: LineSegment StartX=1 StartY=-4.89898 StartZ=0 EndX=1 EndY=-3.89898 EndZ=0
    g4: LineSegment StartX=-1 StartY=-3.89898 StartZ=0 EndX=-1 EndY=-4.89898 EndZ=0
    g5: ArcOfCircle CenterX=0 CenterY=0 CenterZ=0 NormalX=0 NormalY=0 NormalZ=1 Radius=15 StartAngle=4.71239 EndAngle=9.42478
    g6: LineSegment StartX=0 StartY=-15 StartZ=0 EndX=-9.99998 EndY=-15 EndZ=0
    g7: LineSegment StartX=-15 StartY=0 StartZ=0 EndX=-15 EndY=-10 EndZ=0
  constraints (24):
    c: PointOnObject(g5,g-1)
    c: PointOnObject(g5,g-2)
    c: Coincident(g5,g-1)
    c: Coincident(g6,g5)
    c: Horizontal(g6)
    c: Coincident(g7,g5)
    c: Vertical(g7)
    c: Coincident(g2,g6)
    c: Coincident(g2,g7)
    c: Symmetric(g1,g1,g-2)
    c: DistanceX(g1,g1) = 2
    c: DistanceY(g3,g3) = 1
    c: Coincident(g0,g3)
    c: Vertical(g3)
    c: Coincident(g1,g3)
    c: Coincident(g1,g4)
    c: Coincident(g0,g4)
    c: Vertical(g4)
    c: Coincident(g0,g5)
    c: Radius(g0) = 5
    c: Radius(g5) = 15
    c: Tangent(g2,g6)
    c: Tangent(g7,g2)
    c: DistanceX(g2,g-1) = 10
FEATURE [PartDesign::Pad] Pad012001003  label="Rotor001"
  Length = 10
  Length2 = 100
  Midplane = true
  Placement = pos=(56,0,11) rot=(0,0,1;0rad)
  Sketch = -> Sketch033
  Type = 0
FEATURE [Part::Feature] Pad012001003001  label="Rotor002"
  Placement = pos=(56,0,11) rot=(0,0,1;0rad)
  shape: bbox 30 x 30 x 10 mm, 10 faces (baked)
FEATURE [Part::MultiFuse] Fusion006002002002002002002002005002002
  Shapes = -> [Pad012001003001,Fusion006002002002002002002002005001]
FEATURE [Part::Feature] Fusion006002002002002002002002005002002001  label="SecondaryShaft"
  shape: bbox 79.74 x 80.01 x 190 mm, 380 faces (baked)
FEATURE [Sketcher::SketchObject] Sketch034  label="Valve2CalculationSketch"
  Placement = pos=(56,0,11) rot=(0,0,1;0rad)
  sketch-geometry (11):
    g0: ArcOfCircle CenterX=0 CenterY=0 CenterZ=0 NormalX=0 NormalY=0 NormalZ=1 Radius=5 StartAngle=4.91375 EndAngle=10.7942
    g1: LineSegment StartX=-1 StartY=-3.89898 StartZ=0 EndX=1 EndY=-3.89898 EndZ=0
    g2: ArcOfCircle CenterX=-10 CenterY=-10 CenterZ=0 NormalX=0 NormalY=0 NormalZ=1 Radius=5 StartAngle=3.14159 EndAngle=4.71239
    g3: LineSegment StartX=1 StartY=-4.89898 StartZ=0 EndX=1 EndY=-3.89898 EndZ=0
    g4: LineSegment StartX=-1 StartY=-3.89898 StartZ=0 EndX=-1 EndY=-4.89898 EndZ=0
    g5: ArcOfCircle CenterX=0 CenterY=0 CenterZ=0 NormalX=0 NormalY=0 NormalZ=1 Radius=15 StartAngle=4.71239 EndAngle=9.42478
    g6: LineSegment StartX=0 StartY=-15 StartZ=0 EndX=-10 EndY=-15 EndZ=0
    g7: LineSegment StartX=-15 StartY=0 StartZ=0 EndX=-15 EndY=-10 EndZ=0
    g8: LineSegment [constr] StartX=0 StartY=0 StartZ=0 EndX=-9.74111 EndY=-15 EndZ=0
    g9: LineSegment [constr] StartX=0 StartY=0 StartZ=0 EndX=-14.9986 EndY=-10.1167 EndZ=0
    g10: LineSegment [constr] StartX=0 StartY=0 StartZ=0 EndX=-15 EndY=-0.261826 EndZ=0
  constraints (36):
    c: PointOnObject(g5,g-1)
    c: PointOnObject(g5,g-2)
    c: Coincident(g5,g-1)
    c: Coincident(g6,g5)
    c: Horizontal(g6)
    c: Coincident(g7,g5)
    c: Vertical(g7)
    c: Coincident(g2,g6)
    c: Coincident(g2,g7)
    c: Symmetric(g1,g1,g-2)
    c: DistanceX(g1,g1) = 2
    c: DistanceY(g3,g3) = 1
    c: Coincident(g0,g3)
    c: Vertical(g3)
    c: Coincident(g1,g3)
    c: Coincident(g1,g4)
    c: Coincident(g0,g4)
    c: Vertical(g4)
    c: Coincident(g0,g5)
    c: Radius(g0) = 5
    c: Radius(g5) = 15
    c: Tangent(g2,g6)
    c: Tangent(g7,g2)
    c: DistanceX(g2,g-1) = 10
    c: Coincident(g8,g-1)
    c: PointOnObject(g8,g6)
    c: Angle(g-2,g8) = 2.56563
    c: Coincident(g9,g-1)
    c: PointOnObject(g9,g2)
    c: Angle(g-2,g9) = 2.16421
    c: Coincident(g10,g-1)
    c: PointOnObject(g10,g7)
    c: Angle(g-2,g10) = 1.58825
    c: Distance(g8) = 17.8854
    c: Distance(g9) = 18.0916
    c: Distance(g10) = 15.0023
FEATURE [App::DocumentObjectGroup] Group014  label="Valve2"
  Group = -> [Revolution005005002,Sketch032,Pad012001003,Sketch034]
FEATURE [App::DocumentObjectGroup] Group  label="Valves"
  Group = -> [Group011,Group014]
FEATURE [Part::Feature] Revolution005005002003001  label="Valve2RodFinal"
  Placement = pos=(71,0,11) rot=(0,0,1;0rad)
  shape: bbox 45 x 10 x 10 mm, 7 faces (baked)
FEATURE [Part::Cylinder] Cylinder002  label="ExaustHole"
  Angle = 360
  Height = 34
  Placement = pos=(124,35,-34) rot=(1,0,0;1.5708rad)
  Radius = 5
FEATURE [Part::Cut] Cut004  label="HeadWithExaustHole"
  Base = -> Cut003
  Tool = -> Cylinder002
FEATURE [Sketcher::SketchObject] Sketch035
  Placement = pos=(124,35,-34) rot=(0.57735,0.57735,0.57735;2.0944rad)
  sketch-geometry (8):
    g0: LineSegment StartX=0 StartY=0 StartZ=0 EndX=19.5671 EndY=0 EndZ=0
    g1: ArcOfCircle CenterX=19.5671 CenterY=23.2183 CenterZ=0 NormalX=0 NormalY=0 NormalZ=1 Radius=23.2183 StartAngle=4.71239 EndAngle=6.28319
    g2: LineSegment [constr] StartX=19.5671 StartY=23.2183 StartZ=0 EndX=19.5671 EndY=0 EndZ=0
    g3: LineSegment [constr] StartX=19.5671 StartY=23.2183 StartZ=0 EndX=42.7854 EndY=23.2183 EndZ=0
    g4: LineSegment StartX=42.7854 StartY=23.2183 StartZ=0 EndX=42.7854 EndY=65.5979 EndZ=0
    g5: ArcOfCircle CenterX=71.6587 CenterY=65.5979 CenterZ=0 NormalX=0 NormalY=0 NormalZ=1 Radius=28.8733 StartAngle=1.5708 EndAngle=3.14159
    g6: LineSegment [constr] StartX=42.7854 StartY=65.5979 StartZ=0 EndX=71.6587 EndY=65.5979 EndZ=0
    g7: LineSegment [constr] StartX=71.6587 StartY=65.5979 StartZ=0 EndX=71.6587 EndY=94.4712 EndZ=0
  constraints (18):
    c: Coincident(g0,g-1)
    c: PointOnObject(g0,g-1)
    c: Coincident(g1,g0)
    c: Coincident(g2,g1)
    c: Coincident(g2,g0)
    c: Perpendicular(g2,g0)
    c: Coincident(g3,g1)
    c: Coincident(g3,g1)
    c: Perpendicular(g2,g3)
    c: Coincident(g4,g1)
    c: Vertical(g4)
    c: Coincident(g5,g4)
    c: Coincident(g6,g5)
    c: Coincident(g4,g6)
    c: Horizontal(g6)
    c: Coincident(g7,g5)
    c: Vertical(g7)
    c: Coincident(g5,g7)
FEATURE [Sketcher::SketchObject] Sketch036
  Placement = pos=(124,35,-34) rot=(1,0,0;1.5708rad)
  sketch-geometry (1):
    g0: Circle CenterX=0 CenterY=0 CenterZ=0 NormalX=0 NormalY=0 NormalZ=1 Radius=5
  constraints (2):
    c: Coincident(g0,g-1)
    c: Radius(g0) = 5
FEATURE [Part::Feature] Sketch035001
  Placement = pos=(124,35,-34) rot=(0.57735,0.57735,0.57735;2.0944rad)
  shape: bbox 2e-07 x 71.66 x 94.47 mm, 0 faces, 0 solids (baked)
FEATURE [Part::Part2DObjectPython] Circle  # Draft 2D object (typed FeaturePython)
  FirstAngle = 0
  LastAngle = 0
  MakeFace = true
  Placement = pos=(124,35,-34) rot=(1,0,0;1.5708rad)
  Radius = 5
FEATURE [Part::Sweep] Sweep  label="Pipe"
  Frenet = false
  Sections = -> [Circle]
  Solid = false
  Spine = -> Sketch035001 [Edge1,Edge2,Edge3,Edge4]
  Transition = 1
FEATURE [Sketcher::SketchObject] Sketch035002  label="PipeHolderSketch"
  Placement = pos=(124,35,-34) rot=(1,0,0;1.5708rad)
  sketch-geometry (11):
    g0: Circle CenterX=0 CenterY=0 CenterZ=0 NormalX=0 NormalY=0 NormalZ=1 Radius=5
    g1: ArcOfCircle CenterX=0 CenterY=0 CenterZ=0 NormalX=0 NormalY=0 NormalZ=1 Radius=7.46395 StartAngle=1.95273 EndAngle=4.37836
    g2: LineSegment StartX=-2.78191 StartY=6.92614 StartZ=0 EndX=-2.78191 EndY=9.7903 EndZ=0
    g3: LineSegment StartX=-2.44705 StartY=-7.05141 StartZ=0 EndX=-2.44705 EndY=-9.91557 EndZ=0
    g4: LineSegment StartX=2.44705 StartY=-7.05141 StartZ=0 EndX=2.44705 EndY=-9.91557 EndZ=0
    g5: ArcOfCircle CenterX=0 CenterY=0 CenterZ=0 NormalX=0 NormalY=0 NormalZ=1 Radius=7.46395 StartAngle=5.04642 EndAngle=7.47205
    g6: LineSegment StartX=2.78191 StartY=6.92614 StartZ=0 EndX=2.78191 EndY=9.7903 EndZ=0
    g7: ArcOfCircle CenterX=0 CenterY=7.34811 CenterZ=0 NormalX=0 NormalY=0 NormalZ=1 Radius=3.7018 StartAngle=0.720459 EndAngle=2.42113
    g8: ArcOfCircle CenterX=0 CenterY=-7.37194 CenterZ=0 NormalX=0 NormalY=0 NormalZ=1 Radius=3.52961 StartAngle=3.94634 EndAngle=5.47844
    g9: Circle CenterX=0 CenterY=8.74403 CenterZ=0 NormalX=0 NormalY=0 NormalZ=1 Radius=1.5
    g10: Circle CenterX=0 CenterY=-8.74403 CenterZ=0 NormalX=0 NormalY=0 NormalZ=1 Radius=1.5
  constraints (27):
    c: Coincident(g0,g-1)
    c: Radius(g0) = 5
    c: Coincident(g1,g-1)
    c: Coincident(g2,g1)
    c: Vertical(g2)
    c: Coincident(g3,g1)
    c: Vertical(g3)
    c: Vertical(g4)
    c: Coincident(g5,g-1)
    c: Coincident(g5,g4)
    c: Coincident(g6,g5)
    c: Vertical(g6)
    c: PointOnObject(g7,g-2)
    c: Coincident(g7,g2)
    c: Coincident(g7,g6)
    c: PointOnObject(g8,g-2)
    c: Coincident(g8,g3)
    c: Coincident(g8,g4)
    c: Symmetric(g1,g4,g-2)
    c: Equal(g2,g3)
    c: PointOnObject(g9,g-2)
    c: Radius(g9) = 1.5
    c: Equal(g6,g2)
    c: Equal(g3,g4)
    c: PointOnObject(g10,g-2)
    c: Radius(g10) = 1.5
    c: Symmetric(g10,g9,g-1)
FEATURE [PartDesign::Pad] Pad012001003002  label="PipeHolder"
  Length = 5
  Length2 = 100
  Placement = pos=(124,35,-34) rot=(1,0,0;1.5708rad)
  Reversed = true
  Sketch = -> Sketch035002
  Type = 0
FEATURE [App::DocumentObjectGroup] Group015  label="Exhaust-pipe"
  Group = -> [Sketch035,Sketch036,Sweep,Sketch035001,Pad012001003002]
FEATURE [Sketcher::SketchObject] Sketch035003  label="PipeHolderSketch001"
  Placement = pos=(124,35,-34) rot=(1,0,0;1.5708rad)
  sketch-geometry (11):
    g0: Circle CenterX=0 CenterY=0 CenterZ=0 NormalX=0 NormalY=0 NormalZ=1 Radius=5
    g1: ArcOfCircle CenterX=0 CenterY=0 CenterZ=0 NormalX=0 NormalY=0 NormalZ=1 Radius=7.46395 StartAngle=1.95273 EndAngle=4.37836
    g2: LineSegment StartX=-2.78191 StartY=6.92614 StartZ=0 EndX=-2.78191 EndY=9.7903 EndZ=0
    g3: LineSegment StartX=-2.44705 StartY=-7.05141 StartZ=0 EndX=-2.44705 EndY=-9.91557 EndZ=0
    g4: LineSegment StartX=2.44705 StartY=-7.05141 StartZ=0 EndX=2.44705 EndY=-9.91557 EndZ=0
    g5: ArcOfCircle CenterX=0 CenterY=0 CenterZ=0 NormalX=0 NormalY=0 NormalZ=1 Radius=7.46395 StartAngle=5.04642 EndAngle=7.47205
    g6: LineSegment StartX=2.78191 StartY=6.92614 StartZ=0 EndX=2.78191 EndY=9.7903 EndZ=0
    g7: ArcOfCircle CenterX=0 CenterY=7.34811 CenterZ=0 NormalX=0 NormalY=0 NormalZ=1 Radius=3.7018 StartAngle=0.720459 EndAngle=2.42113
    g8: ArcOfCircle CenterX=0 CenterY=-7.37194 CenterZ=0 NormalX=0 NormalY=0 NormalZ=1 Radius=3.52961 StartAngle=3.94634 EndAngle=5.47844
    g9: Circle CenterX=0 CenterY=8.74403 CenterZ=0 NormalX=0 NormalY=0 NormalZ=1 Radius=1.5
    g10: Circle CenterX=0 CenterY=-8.74403 CenterZ=0 NormalX=0 NormalY=0 NormalZ=1 Radius=1.5
  constraints (27):
    c: Coincident(g0,g-1)
    c: Radius(g0) = 5
    c: Coincident(g1,g-1)
    c: Coincident(g2,g1)
    c: Vertical(g2)
    c: Coincident(g3,g1)
    c: Vertical(g3)
    c: Vertical(g4)
    c: Coincident(g5,g-1)
    c: Coincident(g5,g4)
    c: Coincident(g6,g5)
    c: Vertical(g6)
    c: PointOnObject(g7,g-2)
    c: Coincident(g7,g2)
    c: Coincident(g7,g6)
    c: PointOnObject(g8,g-2)
    c: Coincident(g8,g3)
    c: Coincident(g8,g4)
    c: Symmetric(g1,g4,g-2)
    c: Equal(g2,g3)
    c: PointOnObject(g9,g-2)
    c: Radius(g9) = 1.5
    c: Equal(g6,g2)
    c: Equal(g3,g4)
    c: PointOnObject(g10,g-2)
    c: Radius(g10) = 1.5
    c: Symmetric(g10,g9,g-1)
FEATURE [PartDesign::Pad] Pad012001003003  label="PipeHolder001"
  Length = 15
  Length2 = 100
  Placement = pos=(124,35,-34) rot=(1,0,0;1.5708rad)
  Sketch = -> Sketch035003
  Type = 0
FEATURE [Part::MultiFuse] Fusion006002002002002002002002005002002002  label="HeadWithExaustPipeHolder"
  Shapes = -> [Cut004,Pad012001003003]
FEATURE [Sketcher::SketchObject] Sketch035004  label="PipeHolderSketch002"
  Placement = pos=(124,35,-34) rot=(1,0,0;1.5708rad)
  sketch-geometry (11):
    g0: Circle CenterX=0 CenterY=0 CenterZ=0 NormalX=0 NormalY=0 NormalZ=1 Radius=5
    g1: ArcOfCircle CenterX=0 CenterY=0 CenterZ=0 NormalX=0 NormalY=0 NormalZ=1 Radius=7.46395 StartAngle=1.95273 EndAngle=4.37836
    g2: LineSegment StartX=-2.78191 StartY=6.92614 StartZ=0 EndX=-2.78191 EndY=9.7903 EndZ=0
    g3: LineSegment StartX=-2.44705 StartY=-7.05141 StartZ=0 EndX=-2.44705 EndY=-9.91557 EndZ=0
    g4: LineSegment StartX=2.44705 StartY=-7.05141 StartZ=0 EndX=2.44705 EndY=-9.91557 EndZ=0
    g5: ArcOfCircle CenterX=0 CenterY=0 CenterZ=0 NormalX=0 NormalY=0 NormalZ=1 Radius=7.46395 StartAngle=5.04642 EndAngle=7.47205
    g6: LineSegment StartX=2.78191 StartY=6.92614 StartZ=0 EndX=2.78191 EndY=9.7903 EndZ=0
    g7: ArcOfCircle CenterX=0 CenterY=7.34811 CenterZ=0 NormalX=0 NormalY=0 NormalZ=1 Radius=3.7018 StartAngle=0.720459 EndAngle=2.42113
    g8: ArcOfCircle CenterX=0 CenterY=-7.37194 CenterZ=0 NormalX=0 NormalY=0 NormalZ=1 Radius=3.52961 StartAngle=3.94634 EndAngle=5.47844
    g9: Circle CenterX=0 CenterY=8.74403 CenterZ=0 NormalX=0 NormalY=0 NormalZ=1 Radius=1.5
    g10: Circle CenterX=0 CenterY=-8.74403 CenterZ=0 NormalX=0 NormalY=0 NormalZ=1 Radius=1.5
  constraints (27):
    c: Coincident(g0,g-1)
    c: Radius(g0) = 5
    c: Coincident(g1,g-1)
    c: Coincident(g2,g1)
    c: Vertical(g2)
    c: Coincident(g3,g1)
    c: Vertical(g3)
    c: Vertical(g4)
    c: Coincident(g5,g-1)
    c: Coincident(g5,g4)
    c: Coincident(g6,g5)
    c: Vertical(g6)
    c: PointOnObject(g7,g-2)
    c: Coincident(g7,g2)
    c: Coincident(g7,g6)
    c: PointOnObject(g8,g-2)
    c: Coincident(g8,g3)
    c: Coincident(g8,g4)
    c: Symmetric(g1,g4,g-2)
    c: Equal(g2,g3)
    c: PointOnObject(g9,g-2)
    c: Radius(g9) = 1.5
    c: Equal(g6,g2)
    c: Equal(g3,g4)
    c: PointOnObject(g10,g-2)
    c: Radius(g10) = 1.5
    c: Symmetric(g10,g9,g-1)
FEATURE [Part::Cylinder] Cylinder003  label="IntakeHole"
  Angle = 360
  Height = 34
  Placement = pos=(124,0,-99) rot=(0,0,1;0rad)
  Radius = 5
FEATURE [Part::Cut] Cut005
  Base = -> Fusion006002002002002002002002005002002002
  Tool = -> Cylinder003
FEATURE [Sketcher::SketchObject] Sketch035005  label="CarburatorHolderSketch"
  Placement = pos=(124,35,-34) rot=(1,0,0;1.5708rad)
  sketch-geometry (11):
    g0: Circle CenterX=0 CenterY=0 CenterZ=0 NormalX=0 NormalY=0 NormalZ=1 Radius=5
    g1: ArcOfCircle CenterX=0 CenterY=0 CenterZ=0 NormalX=0 NormalY=0 NormalZ=1 Radius=7.46395 StartAngle=1.95273 EndAngle=4.37836
    g2: LineSegment StartX=-2.78191 StartY=6.92614 StartZ=0 EndX=-2.78191 EndY=9.7903 EndZ=0
    g3: LineSegment StartX=-2.44705 StartY=-7.05141 StartZ=0 EndX=-2.44705 EndY=-9.91557 EndZ=0
    g4: LineSegment StartX=2.44705 StartY=-7.05141 StartZ=0 EndX=2.44705 EndY=-9.91557 EndZ=0
    g5: ArcOfCircle CenterX=0 CenterY=0 CenterZ=0 NormalX=0 NormalY=0 NormalZ=1 Radius=7.46395 StartAngle=5.04642 EndAngle=7.47205
    g6: LineSegment StartX=2.78191 StartY=6.92614 StartZ=0 EndX=2.78191 EndY=9.7903 EndZ=0
    g7: ArcOfCircle CenterX=0 CenterY=7.34811 CenterZ=0 NormalX=0 NormalY=0 NormalZ=1 Radius=3.7018 StartAngle=0.720459 EndAngle=2.42113
    g8: ArcOfCircle CenterX=0 CenterY=-7.37194 CenterZ=0 NormalX=0 NormalY=0 NormalZ=1 Radius=3.52961 StartAngle=3.94634 EndAngle=5.47844
    g9: Circle CenterX=0 CenterY=8.74403 CenterZ=0 NormalX=0 NormalY=0 NormalZ=1 Radius=1.5
    g10: Circle CenterX=0 CenterY=-8.74403 CenterZ=0 NormalX=0 NormalY=0 NormalZ=1 Radius=1.5
  constraints (27):
    c: Coincident(g0,g-1)
    c: Radius(g0) = 5
    c: Coincident(g1,g-1)
    c: Coincident(g2,g1)
    c: Vertical(g2)
    c: Coincident(g3,g1)
    c: Vertical(g3)
    c: Vertical(g4)
    c: Coincident(g5,g-1)
    c: Coincident(g5,g4)
    c: Coincident(g6,g5)
    c: Vertical(g6)
    c: PointOnObject(g7,g-2)
    c: Coincident(g7,g2)
    c: Coincident(g7,g6)
    c: PointOnObject(g8,g-2)
    c: Coincident(g8,g3)
    c: Coincident(g8,g4)
    c: Symmetric(g1,g4,g-2)
    c: Equal(g2,g3)
    c: PointOnObject(g9,g-2)
    c: Radius(g9) = 1.5
    c: Equal(g6,g2)
    c: Equal(g3,g4)
    c: PointOnObject(g10,g-2)
    c: Radius(g10) = 1.5
    c: Symmetric(g10,g9,g-1)
FEATURE [PartDesign::Pad] Pad012001003004  label="CarburatorHolder"
  Length = 10
  Length2 = 100
  Placement = pos=(124,35,-34) rot=(1,0,0;1.5708rad)
  Reversed = true
  Sketch = -> Sketch035005
  Type = 0
FEATURE [Part::Feature] Pad012001003004001  label="CarburatorHolderFinal"
  Placement = pos=(124,0,-82) rot=(0,0,1;0rad)
  shape: bbox 14.93 x 21.95 x 10 mm, 13 faces (baked)
FEATURE [Part::MultiFuse] Fusion006002002002002002002002005002002003  label="HeadFinal"
  Shapes = -> [Pad012001003004001,Cut005]
FEATURE [App::DocumentObjectGroup] Group013  label="CylinderHead"
  Group = -> [Pad012001003004,Fusion006002002002002002002002005002002003]
FEATURE [Sketcher::SketchObject] Sketch035006
  Placement = pos=(0,0,0) rot=(-1,0,0;4.71239rad)
  sketch-geometry (8):
    g0: LineSegment [constr] StartX=157.5 StartY=0.293006 StartZ=0 EndX=157.5 EndY=-12.5 EndZ=0
    g1: LineSegment [constr] StartX=157.5 StartY=-12.5 StartZ=0 EndX=157.5 EndY=-25.293 EndZ=0
    g2: Circle CenterX=157.5 CenterY=-12.5 CenterZ=0 NormalX=0 NormalY=0 NormalZ=1 Radius=1.5
    g3: ArcOfCircle CenterX=157.5 CenterY=-25.293 CenterZ=0 NormalX=0 NormalY=0 NormalZ=1 Radius=5.1 StartAngle=1.97377 EndAngle=6.28319
    g4: ArcOfCircle CenterX=157.5 CenterY=0.293006 CenterZ=0 NormalX=0 NormalY=0 NormalZ=1 Radius=7.55175 StartAngle=1.19601 EndAngle=4.30386
    g5: LineSegment StartX=154.5 StartY=-6.63728 StartZ=0 EndX=155.5 EndY=-20.6015 EndZ=0
    g6: LineSegment StartX=162.6 StartY=-25.293 StartZ=0 EndX=160.264 EndY=7.32056 EndZ=0
    g7: LineSegment [constr] StartX=157.5 StartY=-25.293 StartZ=0 EndX=162.6 EndY=-25.293 EndZ=0
  constraints (23):
    c: Vertical(g0)
    c: Coincident(g1,g0)
    c: Vertical(g1)
    c: Equal(g0,g1)
    c: Coincident(g2,g0)
    c: Coincident(g3,g1)
    c: Coincident(g4,g0)
    c: Coincident(g5,g4)
    c: Coincident(g5,g3)
    c: Coincident(g6,g3)
    c: Parallel(g6,g5)
    c: Radius(g2) = 1.5
    c: Radius(g3) = 5.1
    c: Radius(g4) = 7.55175
    c: Distance(g5) = 14
    c: DistanceX(g4,g0) = 3
    c: Coincident(g7,g1)
    c: Coincident(g7,g3)
    c: Perpendicular(g7,g1)
    c: DistanceX(g3,g1) = 2
    c: Coincident(g4,g6)
    c: DistanceX(g-1,g0) = 157.5
    c: DistanceY(g0,g-1) = 12.5
FEATURE [PartDesign::Pad] Pad012001003004002  label="ExaustValveLever"
  Length = 10
  Length2 = 100
  Midplane = true
  Placement = pos=(0,0,0) rot=(-1,0,0;4.71239rad)
  Sketch = -> Sketch035006
  Type = 0
FEATURE [App::DocumentObjectGroup] Group016  label="Valve-Levers"
  Group = -> [Pad012001003004002]
FEATURE [Part::Feature] Revolution005005002003002  label="Valve1RodFinal"
  Placement = pos=(71,0,0) rot=(0,0,1;0rad)
  shape: bbox 79 x 10 x 10 mm, 7 faces (baked)
FEATURE [Part::Feature] Pad012001003004002001001  label="ExaustValveLeverFinal"
  shape: bbox 12.65 x 10 x 38.24 mm, 7 faces (baked)
